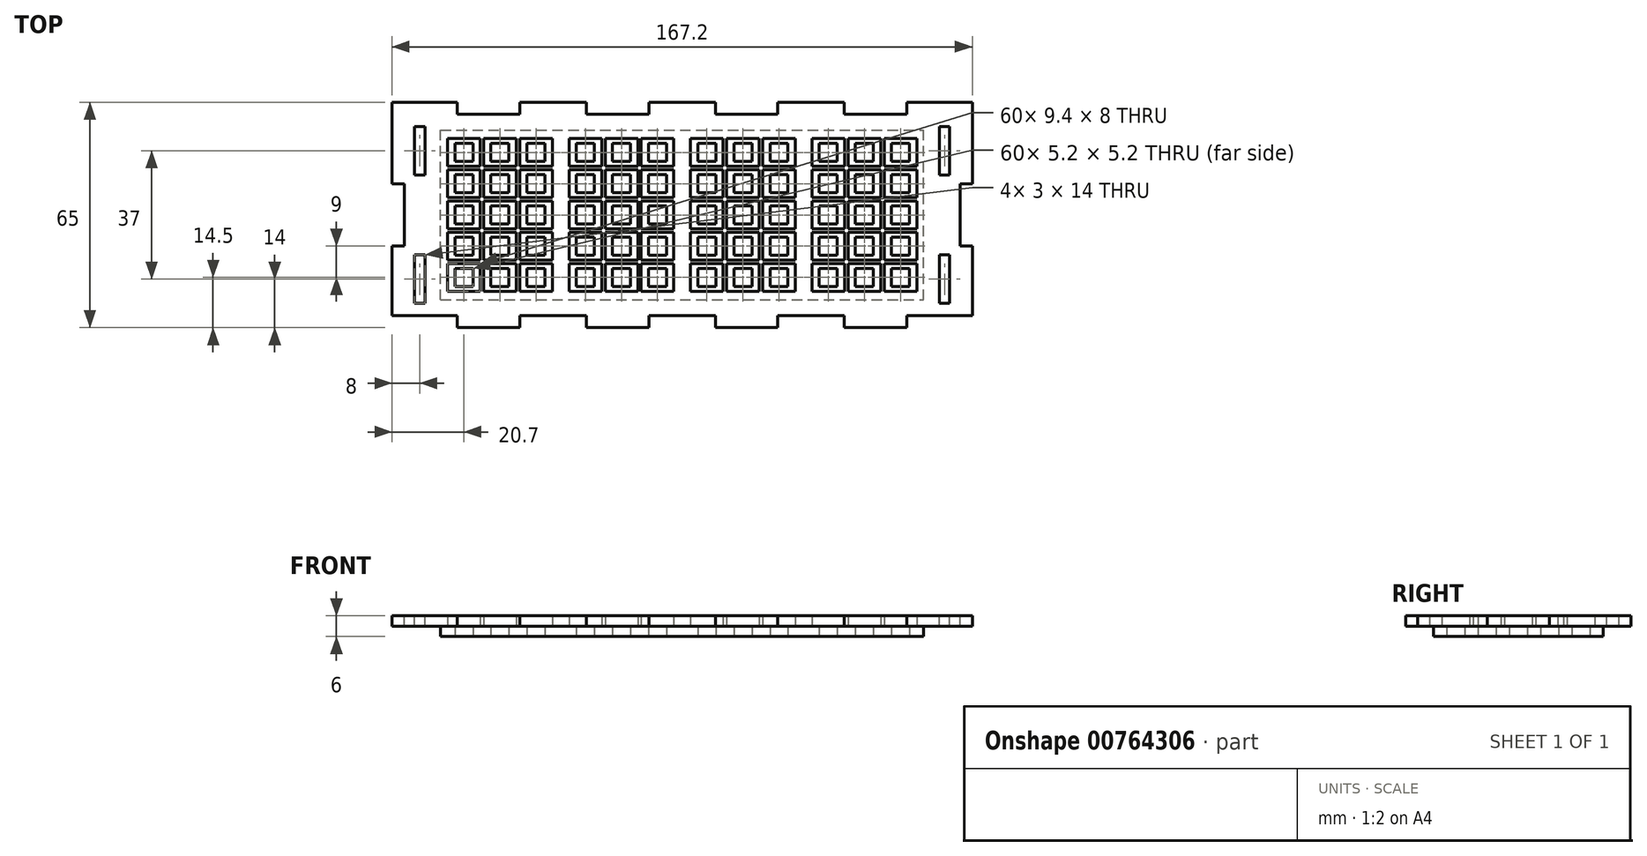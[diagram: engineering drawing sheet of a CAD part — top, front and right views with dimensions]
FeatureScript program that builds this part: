
annotation { "Feature Type Name" : "Feature", "Feature Type Description" : "" }
export const myFeature = defineFeature(function(context is Context, id is Id, definition is map)
    precondition{}
    {
        {
            var Q0;
            Q0=qCreatedBy(makeId("Top.planeOp"),FACE);
            var sketch = newSketch(context, id + "F0", { "sketchPlane" : qUnion([Q0])});
            skLineSegment(sketch, "E0.bottom", {"start": v(0, 0) * mm, "end": v(139.2, 0) * mm});
            skLineSegment(sketch, "E0.left", {"start": v(0, 0) * mm, "end": v(0, 49) * mm});
            skLineSegment(sketch, "E0.right", {"start": v(139.2, 0) * mm, "end": v(139.2, 49) * mm});
            skLineSegment(sketch, "E1.bottom", {"start": v(4.1, 3.9) * mm, "end": v(9.3, 3.9) * mm});
            skLineSegment(sketch, "E1.top", {"start": v(4.1, 9.1) * mm, "end": v(9.3, 9.1) * mm});
            skLineSegment(sketch, "E1.left", {"start": v(4.1, 3.9) * mm, "end": v(4.1, 9.1) * mm});
            skLineSegment(sketch, "E1.right", {"start": v(9.3, 3.9) * mm, "end": v(9.3, 9.1) * mm});
            skLineSegment(sketch, "E2.bottom", {"start": v(39.1, 3.9) * mm, "end": v(44.3, 3.9) * mm});
            skLineSegment(sketch, "E2.top", {"start": v(39.1, 9.1) * mm, "end": v(44.3, 9.1) * mm});
            skLineSegment(sketch, "E2.left", {"start": v(39.1, 3.9) * mm, "end": v(39.1, 9.1) * mm});
            skLineSegment(sketch, "E2.right", {"start": v(44.3, 3.9) * mm, "end": v(44.3, 9.1) * mm});
            skLineSegment(sketch, "E3", {"start": v(0, 49) * mm, "end": v(139.2, 49) * mm});
            skLineSegment(sketch, "E4.bottom", {"start": v(74.1, 3.9) * mm, "end": v(79.3, 3.9) * mm});
            skLineSegment(sketch, "E4.top", {"start": v(74.1, 9.1) * mm, "end": v(79.3, 9.1) * mm});
            skLineSegment(sketch, "E4.left", {"start": v(74.1, 3.9) * mm, "end": v(74.1, 9.1) * mm});
            skLineSegment(sketch, "E4.right", {"start": v(79.3, 3.9) * mm, "end": v(79.3, 9.1) * mm});
            skLineSegment(sketch, "E5.bottom", {"start": v(109.1, 3.9) * mm, "end": v(114.3, 3.9) * mm});
            skLineSegment(sketch, "E5.top", {"start": v(109.1, 9.1) * mm, "end": v(114.3, 9.1) * mm});
            skLineSegment(sketch, "E5.left", {"start": v(109.1, 3.9) * mm, "end": v(109.1, 9.1) * mm});
            skLineSegment(sketch, "E5.right", {"start": v(114.3, 3.9) * mm, "end": v(114.3, 9.1) * mm});
            skLineSegment(sketch, "E6.0.1.0", {"start": v(39.1, 12.9) * mm, "end": v(44.3, 12.9) * mm});
            skLineSegment(sketch, "E6.0.1.1", {"start": v(74.1, 12.9) * mm, "end": v(74.1, 18.1) * mm});
            skLineSegment(sketch, "E6.0.1.2", {"start": v(74.1, 18.1) * mm, "end": v(79.3, 18.1) * mm});
            skLineSegment(sketch, "E6.0.1.3", {"start": v(9.3, 12.9) * mm, "end": v(9.3, 18.1) * mm});
            skLineSegment(sketch, "E6.0.1.4", {"start": v(74.1, 12.9) * mm, "end": v(79.3, 12.9) * mm});
            skLineSegment(sketch, "E6.0.1.5", {"start": v(44.3, 12.9) * mm, "end": v(44.3, 18.1) * mm});
            skLineSegment(sketch, "E6.0.1.6", {"start": v(39.1, 12.9) * mm, "end": v(39.1, 18.1) * mm});
            skLineSegment(sketch, "E6.0.1.7", {"start": v(109.1, 12.9) * mm, "end": v(114.3, 12.9) * mm});
            skLineSegment(sketch, "E6.0.1.8", {"start": v(4.1, 12.9) * mm, "end": v(9.3, 12.9) * mm});
            skLineSegment(sketch, "E6.0.1.9", {"start": v(114.3, 12.9) * mm, "end": v(114.3, 18.1) * mm});
            skLineSegment(sketch, "E6.0.1.10", {"start": v(4.1, 12.9) * mm, "end": v(4.1, 18.1) * mm});
            skLineSegment(sketch, "E6.0.1.11", {"start": v(79.3, 12.9) * mm, "end": v(79.3, 18.1) * mm});
            skLineSegment(sketch, "E6.0.1.12", {"start": v(109.1, 12.9) * mm, "end": v(109.1, 18.1) * mm});
            skLineSegment(sketch, "E6.0.1.13", {"start": v(39.1, 18.1) * mm, "end": v(44.3, 18.1) * mm});
            skLineSegment(sketch, "E6.0.1.14", {"start": v(4.1, 18.1) * mm, "end": v(9.3, 18.1) * mm});
            skLineSegment(sketch, "E6.0.1.15", {"start": v(109.1, 18.1) * mm, "end": v(114.3, 18.1) * mm});
            skLineSegment(sketch, "E6.0.2.0", {"start": v(39.1, 21.9) * mm, "end": v(44.3, 21.9) * mm});
            skLineSegment(sketch, "E6.0.2.1", {"start": v(74.1, 21.9) * mm, "end": v(74.1, 27.1) * mm});
            skLineSegment(sketch, "E6.0.2.2", {"start": v(74.1, 27.1) * mm, "end": v(79.3, 27.1) * mm});
            skLineSegment(sketch, "E6.0.2.3", {"start": v(9.3, 21.9) * mm, "end": v(9.3, 27.1) * mm});
            skLineSegment(sketch, "E6.0.2.4", {"start": v(74.1, 21.9) * mm, "end": v(79.3, 21.9) * mm});
            skLineSegment(sketch, "E6.0.2.5", {"start": v(44.3, 21.9) * mm, "end": v(44.3, 27.1) * mm});
            skLineSegment(sketch, "E6.0.2.6", {"start": v(39.1, 21.9) * mm, "end": v(39.1, 27.1) * mm});
            skLineSegment(sketch, "E6.0.2.7", {"start": v(109.1, 21.9) * mm, "end": v(114.3, 21.9) * mm});
            skLineSegment(sketch, "E6.0.2.8", {"start": v(4.1, 21.9) * mm, "end": v(9.3, 21.9) * mm});
            skLineSegment(sketch, "E6.0.2.9", {"start": v(114.3, 21.9) * mm, "end": v(114.3, 27.1) * mm});
            skLineSegment(sketch, "E6.0.2.10", {"start": v(4.1, 21.9) * mm, "end": v(4.1, 27.1) * mm});
            skLineSegment(sketch, "E6.0.2.11", {"start": v(79.3, 21.9) * mm, "end": v(79.3, 27.1) * mm});
            skLineSegment(sketch, "E6.0.2.12", {"start": v(109.1, 21.9) * mm, "end": v(109.1, 27.1) * mm});
            skLineSegment(sketch, "E6.0.2.13", {"start": v(39.1, 27.1) * mm, "end": v(44.3, 27.1) * mm});
            skLineSegment(sketch, "E6.0.2.14", {"start": v(4.1, 27.1) * mm, "end": v(9.3, 27.1) * mm});
            skLineSegment(sketch, "E6.0.2.15", {"start": v(109.1, 27.1) * mm, "end": v(114.3, 27.1) * mm});
            skLineSegment(sketch, "E6.0.3.0", {"start": v(39.1, 30.9) * mm, "end": v(44.3, 30.9) * mm});
            skLineSegment(sketch, "E6.0.3.1", {"start": v(74.1, 30.9) * mm, "end": v(74.1, 36.1) * mm});
            skLineSegment(sketch, "E6.0.3.2", {"start": v(74.1, 36.1) * mm, "end": v(79.3, 36.1) * mm});
            skLineSegment(sketch, "E6.0.3.3", {"start": v(9.3, 30.9) * mm, "end": v(9.3, 36.1) * mm});
            skLineSegment(sketch, "E6.0.3.4", {"start": v(74.1, 30.9) * mm, "end": v(79.3, 30.9) * mm});
            skLineSegment(sketch, "E6.0.3.5", {"start": v(44.3, 30.9) * mm, "end": v(44.3, 36.1) * mm});
            skLineSegment(sketch, "E6.0.3.6", {"start": v(39.1, 30.9) * mm, "end": v(39.1, 36.1) * mm});
            skLineSegment(sketch, "E6.0.3.7", {"start": v(109.1, 30.9) * mm, "end": v(114.3, 30.9) * mm});
            skLineSegment(sketch, "E6.0.3.8", {"start": v(4.1, 30.9) * mm, "end": v(9.3, 30.9) * mm});
            skLineSegment(sketch, "E6.0.3.9", {"start": v(114.3, 30.9) * mm, "end": v(114.3, 36.1) * mm});
            skLineSegment(sketch, "E6.0.3.10", {"start": v(4.1, 30.9) * mm, "end": v(4.1, 36.1) * mm});
            skLineSegment(sketch, "E6.0.3.11", {"start": v(79.3, 30.9) * mm, "end": v(79.3, 36.1) * mm});
            skLineSegment(sketch, "E6.0.3.12", {"start": v(109.1, 30.9) * mm, "end": v(109.1, 36.1) * mm});
            skLineSegment(sketch, "E6.0.3.13", {"start": v(39.1, 36.1) * mm, "end": v(44.3, 36.1) * mm});
            skLineSegment(sketch, "E6.0.3.14", {"start": v(4.1, 36.1) * mm, "end": v(9.3, 36.1) * mm});
            skLineSegment(sketch, "E6.0.3.15", {"start": v(109.1, 36.1) * mm, "end": v(114.3, 36.1) * mm});
            skLineSegment(sketch, "E6.0.4.0", {"start": v(39.1, 39.9) * mm, "end": v(44.3, 39.9) * mm});
            skLineSegment(sketch, "E6.0.4.1", {"start": v(74.1, 39.9) * mm, "end": v(74.1, 45.1) * mm});
            skLineSegment(sketch, "E6.0.4.2", {"start": v(74.1, 45.1) * mm, "end": v(79.3, 45.1) * mm});
            skLineSegment(sketch, "E6.0.4.3", {"start": v(9.3, 39.9) * mm, "end": v(9.3, 45.1) * mm});
            skLineSegment(sketch, "E6.0.4.4", {"start": v(74.1, 39.9) * mm, "end": v(79.3, 39.9) * mm});
            skLineSegment(sketch, "E6.0.4.5", {"start": v(44.3, 39.9) * mm, "end": v(44.3, 45.1) * mm});
            skLineSegment(sketch, "E6.0.4.6", {"start": v(39.1, 39.9) * mm, "end": v(39.1, 45.1) * mm});
            skLineSegment(sketch, "E6.0.4.7", {"start": v(109.1, 39.9) * mm, "end": v(114.3, 39.9) * mm});
            skLineSegment(sketch, "E6.0.4.8", {"start": v(4.1, 39.9) * mm, "end": v(9.3, 39.9) * mm});
            skLineSegment(sketch, "E6.0.4.9", {"start": v(114.3, 39.9) * mm, "end": v(114.3, 45.1) * mm});
            skLineSegment(sketch, "E6.0.4.10", {"start": v(4.1, 39.9) * mm, "end": v(4.1, 45.1) * mm});
            skLineSegment(sketch, "E6.0.4.11", {"start": v(79.3, 39.9) * mm, "end": v(79.3, 45.1) * mm});
            skLineSegment(sketch, "E6.0.4.12", {"start": v(109.1, 39.9) * mm, "end": v(109.1, 45.1) * mm});
            skLineSegment(sketch, "E6.0.4.13", {"start": v(39.1, 45.1) * mm, "end": v(44.3, 45.1) * mm});
            skLineSegment(sketch, "E6.0.4.14", {"start": v(4.1, 45.1) * mm, "end": v(9.3, 45.1) * mm});
            skLineSegment(sketch, "E6.0.4.15", {"start": v(109.1, 45.1) * mm, "end": v(114.3, 45.1) * mm});
            skLineSegment(sketch, "E6.1.0.0", {"start": v(49.5, 3.9) * mm, "end": v(54.7, 3.9) * mm});
            skLineSegment(sketch, "E6.1.0.1", {"start": v(84.5, 3.9) * mm, "end": v(84.5, 9.1) * mm});
            skLineSegment(sketch, "E6.1.0.2", {"start": v(84.5, 9.1) * mm, "end": v(89.7, 9.1) * mm});
            skLineSegment(sketch, "E6.1.0.3", {"start": v(19.7, 3.9) * mm, "end": v(19.7, 9.1) * mm});
            skLineSegment(sketch, "E6.1.0.4", {"start": v(84.5, 3.9) * mm, "end": v(89.7, 3.9) * mm});
            skLineSegment(sketch, "E6.1.0.5", {"start": v(54.7, 3.9) * mm, "end": v(54.7, 9.1) * mm});
            skLineSegment(sketch, "E6.1.0.6", {"start": v(49.5, 3.9) * mm, "end": v(49.5, 9.1) * mm});
            skLineSegment(sketch, "E6.1.0.7", {"start": v(119.5, 3.9) * mm, "end": v(124.7, 3.9) * mm});
            skLineSegment(sketch, "E6.1.0.8", {"start": v(14.5, 3.9) * mm, "end": v(19.7, 3.9) * mm});
            skLineSegment(sketch, "E6.1.0.9", {"start": v(124.7, 3.9) * mm, "end": v(124.7, 9.1) * mm});
            skLineSegment(sketch, "E6.1.0.10", {"start": v(14.5, 3.9) * mm, "end": v(14.5, 9.1) * mm});
            skLineSegment(sketch, "E6.1.0.11", {"start": v(89.7, 3.9) * mm, "end": v(89.7, 9.1) * mm});
            skLineSegment(sketch, "E6.1.0.12", {"start": v(119.5, 3.9) * mm, "end": v(119.5, 9.1) * mm});
            skLineSegment(sketch, "E6.1.0.13", {"start": v(49.5, 9.1) * mm, "end": v(54.7, 9.1) * mm});
            skLineSegment(sketch, "E6.1.0.14", {"start": v(14.5, 9.1) * mm, "end": v(19.7, 9.1) * mm});
            skLineSegment(sketch, "E6.1.0.15", {"start": v(119.5, 9.1) * mm, "end": v(124.7, 9.1) * mm});
            skLineSegment(sketch, "E6.1.1.0", {"start": v(49.5, 12.9) * mm, "end": v(54.7, 12.9) * mm});
            skLineSegment(sketch, "E6.1.1.1", {"start": v(84.5, 12.9) * mm, "end": v(84.5, 18.1) * mm});
            skLineSegment(sketch, "E6.1.1.2", {"start": v(84.5, 18.1) * mm, "end": v(89.7, 18.1) * mm});
            skLineSegment(sketch, "E6.1.1.3", {"start": v(19.7, 12.9) * mm, "end": v(19.7, 18.1) * mm});
            skLineSegment(sketch, "E6.1.1.4", {"start": v(84.5, 12.9) * mm, "end": v(89.7, 12.9) * mm});
            skLineSegment(sketch, "E6.1.1.5", {"start": v(54.7, 12.9) * mm, "end": v(54.7, 18.1) * mm});
            skLineSegment(sketch, "E6.1.1.6", {"start": v(49.5, 12.9) * mm, "end": v(49.5, 18.1) * mm});
            skLineSegment(sketch, "E6.1.1.7", {"start": v(119.5, 12.9) * mm, "end": v(124.7, 12.9) * mm});
            skLineSegment(sketch, "E6.1.1.8", {"start": v(14.5, 12.9) * mm, "end": v(19.7, 12.9) * mm});
            skLineSegment(sketch, "E6.1.1.9", {"start": v(124.7, 12.9) * mm, "end": v(124.7, 18.1) * mm});
            skLineSegment(sketch, "E6.1.1.10", {"start": v(14.5, 12.9) * mm, "end": v(14.5, 18.1) * mm});
            skLineSegment(sketch, "E6.1.1.11", {"start": v(89.7, 12.9) * mm, "end": v(89.7, 18.1) * mm});
            skLineSegment(sketch, "E6.1.1.12", {"start": v(119.5, 12.9) * mm, "end": v(119.5, 18.1) * mm});
            skLineSegment(sketch, "E6.1.1.13", {"start": v(49.5, 18.1) * mm, "end": v(54.7, 18.1) * mm});
            skLineSegment(sketch, "E6.1.1.14", {"start": v(14.5, 18.1) * mm, "end": v(19.7, 18.1) * mm});
            skLineSegment(sketch, "E6.1.1.15", {"start": v(119.5, 18.1) * mm, "end": v(124.7, 18.1) * mm});
            skLineSegment(sketch, "E6.1.2.0", {"start": v(49.5, 21.9) * mm, "end": v(54.7, 21.9) * mm});
            skLineSegment(sketch, "E6.1.2.1", {"start": v(84.5, 21.9) * mm, "end": v(84.5, 27.1) * mm});
            skLineSegment(sketch, "E6.1.2.2", {"start": v(84.5, 27.1) * mm, "end": v(89.7, 27.1) * mm});
            skLineSegment(sketch, "E6.1.2.3", {"start": v(19.7, 21.9) * mm, "end": v(19.7, 27.1) * mm});
            skLineSegment(sketch, "E6.1.2.4", {"start": v(84.5, 21.9) * mm, "end": v(89.7, 21.9) * mm});
            skLineSegment(sketch, "E6.1.2.5", {"start": v(54.7, 21.9) * mm, "end": v(54.7, 27.1) * mm});
            skLineSegment(sketch, "E6.1.2.6", {"start": v(49.5, 21.9) * mm, "end": v(49.5, 27.1) * mm});
            skLineSegment(sketch, "E6.1.2.7", {"start": v(119.5, 21.9) * mm, "end": v(124.7, 21.9) * mm});
            skLineSegment(sketch, "E6.1.2.8", {"start": v(14.5, 21.9) * mm, "end": v(19.7, 21.9) * mm});
            skLineSegment(sketch, "E6.1.2.9", {"start": v(124.7, 21.9) * mm, "end": v(124.7, 27.1) * mm});
            skLineSegment(sketch, "E6.1.2.10", {"start": v(14.5, 21.9) * mm, "end": v(14.5, 27.1) * mm});
            skLineSegment(sketch, "E6.1.2.11", {"start": v(89.7, 21.9) * mm, "end": v(89.7, 27.1) * mm});
            skLineSegment(sketch, "E6.1.2.12", {"start": v(119.5, 21.9) * mm, "end": v(119.5, 27.1) * mm});
            skLineSegment(sketch, "E6.1.2.13", {"start": v(49.5, 27.1) * mm, "end": v(54.7, 27.1) * mm});
            skLineSegment(sketch, "E6.1.2.14", {"start": v(14.5, 27.1) * mm, "end": v(19.7, 27.1) * mm});
            skLineSegment(sketch, "E6.1.2.15", {"start": v(119.5, 27.1) * mm, "end": v(124.7, 27.1) * mm});
            skLineSegment(sketch, "E6.1.3.0", {"start": v(49.5, 30.9) * mm, "end": v(54.7, 30.9) * mm});
            skLineSegment(sketch, "E6.1.3.1", {"start": v(84.5, 30.9) * mm, "end": v(84.5, 36.1) * mm});
            skLineSegment(sketch, "E6.1.3.2", {"start": v(84.5, 36.1) * mm, "end": v(89.7, 36.1) * mm});
            skLineSegment(sketch, "E6.1.3.3", {"start": v(19.7, 30.9) * mm, "end": v(19.7, 36.1) * mm});
            skLineSegment(sketch, "E6.1.3.4", {"start": v(84.5, 30.9) * mm, "end": v(89.7, 30.9) * mm});
            skLineSegment(sketch, "E6.1.3.5", {"start": v(54.7, 30.9) * mm, "end": v(54.7, 36.1) * mm});
            skLineSegment(sketch, "E6.1.3.6", {"start": v(49.5, 30.9) * mm, "end": v(49.5, 36.1) * mm});
            skLineSegment(sketch, "E6.1.3.7", {"start": v(119.5, 30.9) * mm, "end": v(124.7, 30.9) * mm});
            skLineSegment(sketch, "E6.1.3.8", {"start": v(14.5, 30.9) * mm, "end": v(19.7, 30.9) * mm});
            skLineSegment(sketch, "E6.1.3.9", {"start": v(124.7, 30.9) * mm, "end": v(124.7, 36.1) * mm});
            skLineSegment(sketch, "E6.1.3.10", {"start": v(14.5, 30.9) * mm, "end": v(14.5, 36.1) * mm});
            skLineSegment(sketch, "E6.1.3.11", {"start": v(89.7, 30.9) * mm, "end": v(89.7, 36.1) * mm});
            skLineSegment(sketch, "E6.1.3.12", {"start": v(119.5, 30.9) * mm, "end": v(119.5, 36.1) * mm});
            skLineSegment(sketch, "E6.1.3.13", {"start": v(49.5, 36.1) * mm, "end": v(54.7, 36.1) * mm});
            skLineSegment(sketch, "E6.1.3.14", {"start": v(14.5, 36.1) * mm, "end": v(19.7, 36.1) * mm});
            skLineSegment(sketch, "E6.1.3.15", {"start": v(119.5, 36.1) * mm, "end": v(124.7, 36.1) * mm});
            skLineSegment(sketch, "E6.1.4.0", {"start": v(49.5, 39.9) * mm, "end": v(54.7, 39.9) * mm});
            skLineSegment(sketch, "E6.1.4.1", {"start": v(84.5, 39.9) * mm, "end": v(84.5, 45.1) * mm});
            skLineSegment(sketch, "E6.1.4.2", {"start": v(84.5, 45.1) * mm, "end": v(89.7, 45.1) * mm});
            skLineSegment(sketch, "E6.1.4.3", {"start": v(19.7, 39.9) * mm, "end": v(19.7, 45.1) * mm});
            skLineSegment(sketch, "E6.1.4.4", {"start": v(84.5, 39.9) * mm, "end": v(89.7, 39.9) * mm});
            skLineSegment(sketch, "E6.1.4.5", {"start": v(54.7, 39.9) * mm, "end": v(54.7, 45.1) * mm});
            skLineSegment(sketch, "E6.1.4.6", {"start": v(49.5, 39.9) * mm, "end": v(49.5, 45.1) * mm});
            skLineSegment(sketch, "E6.1.4.7", {"start": v(119.5, 39.9) * mm, "end": v(124.7, 39.9) * mm});
            skLineSegment(sketch, "E6.1.4.8", {"start": v(14.5, 39.9) * mm, "end": v(19.7, 39.9) * mm});
            skLineSegment(sketch, "E6.1.4.9", {"start": v(124.7, 39.9) * mm, "end": v(124.7, 45.1) * mm});
            skLineSegment(sketch, "E6.1.4.10", {"start": v(14.5, 39.9) * mm, "end": v(14.5, 45.1) * mm});
            skLineSegment(sketch, "E6.1.4.11", {"start": v(89.7, 39.9) * mm, "end": v(89.7, 45.1) * mm});
            skLineSegment(sketch, "E6.1.4.12", {"start": v(119.5, 39.9) * mm, "end": v(119.5, 45.1) * mm});
            skLineSegment(sketch, "E6.1.4.13", {"start": v(49.5, 45.1) * mm, "end": v(54.7, 45.1) * mm});
            skLineSegment(sketch, "E6.1.4.14", {"start": v(14.5, 45.1) * mm, "end": v(19.7, 45.1) * mm});
            skLineSegment(sketch, "E6.1.4.15", {"start": v(119.5, 45.1) * mm, "end": v(124.7, 45.1) * mm});
            skLineSegment(sketch, "E6.2.0.0", {"start": v(59.9, 3.9) * mm, "end": v(65.1, 3.9) * mm});
            skLineSegment(sketch, "E6.2.0.1", {"start": v(94.9, 3.9) * mm, "end": v(94.9, 9.1) * mm});
            skLineSegment(sketch, "E6.2.0.2", {"start": v(94.9, 9.1) * mm, "end": v(100.1, 9.1) * mm});
            skLineSegment(sketch, "E6.2.0.3", {"start": v(30.1, 3.9) * mm, "end": v(30.1, 9.1) * mm});
            skLineSegment(sketch, "E6.2.0.4", {"start": v(94.9, 3.9) * mm, "end": v(100.1, 3.9) * mm});
            skLineSegment(sketch, "E6.2.0.5", {"start": v(65.1, 3.9) * mm, "end": v(65.1, 9.1) * mm});
            skLineSegment(sketch, "E6.2.0.6", {"start": v(59.9, 3.9) * mm, "end": v(59.9, 9.1) * mm});
            skLineSegment(sketch, "E6.2.0.7", {"start": v(129.9, 3.9) * mm, "end": v(135.1, 3.9) * mm});
            skLineSegment(sketch, "E6.2.0.8", {"start": v(24.9, 3.9) * mm, "end": v(30.1, 3.9) * mm});
            skLineSegment(sketch, "E6.2.0.9", {"start": v(135.1, 3.9) * mm, "end": v(135.1, 9.1) * mm});
            skLineSegment(sketch, "E6.2.0.10", {"start": v(24.9, 3.9) * mm, "end": v(24.9, 9.1) * mm});
            skLineSegment(sketch, "E6.2.0.11", {"start": v(100.1, 3.9) * mm, "end": v(100.1, 9.1) * mm});
            skLineSegment(sketch, "E6.2.0.12", {"start": v(129.9, 3.9) * mm, "end": v(129.9, 9.1) * mm});
            skLineSegment(sketch, "E6.2.0.13", {"start": v(59.9, 9.1) * mm, "end": v(65.1, 9.1) * mm});
            skLineSegment(sketch, "E6.2.0.14", {"start": v(24.9, 9.1) * mm, "end": v(30.1, 9.1) * mm});
            skLineSegment(sketch, "E6.2.0.15", {"start": v(129.9, 9.1) * mm, "end": v(135.1, 9.1) * mm});
            skLineSegment(sketch, "E6.2.1.0", {"start": v(59.9, 12.9) * mm, "end": v(65.1, 12.9) * mm});
            skLineSegment(sketch, "E6.2.1.1", {"start": v(94.9, 12.9) * mm, "end": v(94.9, 18.1) * mm});
            skLineSegment(sketch, "E6.2.1.2", {"start": v(94.9, 18.1) * mm, "end": v(100.1, 18.1) * mm});
            skLineSegment(sketch, "E6.2.1.3", {"start": v(30.1, 12.9) * mm, "end": v(30.1, 18.1) * mm});
            skLineSegment(sketch, "E6.2.1.4", {"start": v(94.9, 12.9) * mm, "end": v(100.1, 12.9) * mm});
            skLineSegment(sketch, "E6.2.1.5", {"start": v(65.1, 12.9) * mm, "end": v(65.1, 18.1) * mm});
            skLineSegment(sketch, "E6.2.1.6", {"start": v(59.9, 12.9) * mm, "end": v(59.9, 18.1) * mm});
            skLineSegment(sketch, "E6.2.1.7", {"start": v(129.9, 12.9) * mm, "end": v(135.1, 12.9) * mm});
            skLineSegment(sketch, "E6.2.1.8", {"start": v(24.9, 12.9) * mm, "end": v(30.1, 12.9) * mm});
            skLineSegment(sketch, "E6.2.1.9", {"start": v(135.1, 12.9) * mm, "end": v(135.1, 18.1) * mm});
            skLineSegment(sketch, "E6.2.1.10", {"start": v(24.9, 12.9) * mm, "end": v(24.9, 18.1) * mm});
            skLineSegment(sketch, "E6.2.1.11", {"start": v(100.1, 12.9) * mm, "end": v(100.1, 18.1) * mm});
            skLineSegment(sketch, "E6.2.1.12", {"start": v(129.9, 12.9) * mm, "end": v(129.9, 18.1) * mm});
            skLineSegment(sketch, "E6.2.1.13", {"start": v(59.9, 18.1) * mm, "end": v(65.1, 18.1) * mm});
            skLineSegment(sketch, "E6.2.1.14", {"start": v(24.9, 18.1) * mm, "end": v(30.1, 18.1) * mm});
            skLineSegment(sketch, "E6.2.1.15", {"start": v(129.9, 18.1) * mm, "end": v(135.1, 18.1) * mm});
            skLineSegment(sketch, "E6.2.2.0", {"start": v(59.9, 21.9) * mm, "end": v(65.1, 21.9) * mm});
            skLineSegment(sketch, "E6.2.2.1", {"start": v(94.9, 21.9) * mm, "end": v(94.9, 27.1) * mm});
            skLineSegment(sketch, "E6.2.2.2", {"start": v(94.9, 27.1) * mm, "end": v(100.1, 27.1) * mm});
            skLineSegment(sketch, "E6.2.2.3", {"start": v(30.1, 21.9) * mm, "end": v(30.1, 27.1) * mm});
            skLineSegment(sketch, "E6.2.2.4", {"start": v(94.9, 21.9) * mm, "end": v(100.1, 21.9) * mm});
            skLineSegment(sketch, "E6.2.2.5", {"start": v(65.1, 21.9) * mm, "end": v(65.1, 27.1) * mm});
            skLineSegment(sketch, "E6.2.2.6", {"start": v(59.9, 21.9) * mm, "end": v(59.9, 27.1) * mm});
            skLineSegment(sketch, "E6.2.2.7", {"start": v(129.9, 21.9) * mm, "end": v(135.1, 21.9) * mm});
            skLineSegment(sketch, "E6.2.2.8", {"start": v(24.9, 21.9) * mm, "end": v(30.1, 21.9) * mm});
            skLineSegment(sketch, "E6.2.2.9", {"start": v(135.1, 21.9) * mm, "end": v(135.1, 27.1) * mm});
            skLineSegment(sketch, "E6.2.2.10", {"start": v(24.9, 21.9) * mm, "end": v(24.9, 27.1) * mm});
            skLineSegment(sketch, "E6.2.2.11", {"start": v(100.1, 21.9) * mm, "end": v(100.1, 27.1) * mm});
            skLineSegment(sketch, "E6.2.2.12", {"start": v(129.9, 21.9) * mm, "end": v(129.9, 27.1) * mm});
            skLineSegment(sketch, "E6.2.2.13", {"start": v(59.9, 27.1) * mm, "end": v(65.1, 27.1) * mm});
            skLineSegment(sketch, "E6.2.2.14", {"start": v(24.9, 27.1) * mm, "end": v(30.1, 27.1) * mm});
            skLineSegment(sketch, "E6.2.2.15", {"start": v(129.9, 27.1) * mm, "end": v(135.1, 27.1) * mm});
            skLineSegment(sketch, "E6.2.3.0", {"start": v(59.9, 30.9) * mm, "end": v(65.1, 30.9) * mm});
            skLineSegment(sketch, "E6.2.3.1", {"start": v(94.9, 30.9) * mm, "end": v(94.9, 36.1) * mm});
            skLineSegment(sketch, "E6.2.3.2", {"start": v(94.9, 36.1) * mm, "end": v(100.1, 36.1) * mm});
            skLineSegment(sketch, "E6.2.3.3", {"start": v(30.1, 30.9) * mm, "end": v(30.1, 36.1) * mm});
            skLineSegment(sketch, "E6.2.3.4", {"start": v(94.9, 30.9) * mm, "end": v(100.1, 30.9) * mm});
            skLineSegment(sketch, "E6.2.3.5", {"start": v(65.1, 30.9) * mm, "end": v(65.1, 36.1) * mm});
            skLineSegment(sketch, "E6.2.3.6", {"start": v(59.9, 30.9) * mm, "end": v(59.9, 36.1) * mm});
            skLineSegment(sketch, "E6.2.3.7", {"start": v(129.9, 30.9) * mm, "end": v(135.1, 30.9) * mm});
            skLineSegment(sketch, "E6.2.3.8", {"start": v(24.9, 30.9) * mm, "end": v(30.1, 30.9) * mm});
            skLineSegment(sketch, "E6.2.3.9", {"start": v(135.1, 30.9) * mm, "end": v(135.1, 36.1) * mm});
            skLineSegment(sketch, "E6.2.3.10", {"start": v(24.9, 30.9) * mm, "end": v(24.9, 36.1) * mm});
            skLineSegment(sketch, "E6.2.3.11", {"start": v(100.1, 30.9) * mm, "end": v(100.1, 36.1) * mm});
            skLineSegment(sketch, "E6.2.3.12", {"start": v(129.9, 30.9) * mm, "end": v(129.9, 36.1) * mm});
            skLineSegment(sketch, "E6.2.3.13", {"start": v(59.9, 36.1) * mm, "end": v(65.1, 36.1) * mm});
            skLineSegment(sketch, "E6.2.3.14", {"start": v(24.9, 36.1) * mm, "end": v(30.1, 36.1) * mm});
            skLineSegment(sketch, "E6.2.3.15", {"start": v(129.9, 36.1) * mm, "end": v(135.1, 36.1) * mm});
            skLineSegment(sketch, "E6.2.4.0", {"start": v(59.9, 39.9) * mm, "end": v(65.1, 39.9) * mm});
            skLineSegment(sketch, "E6.2.4.1", {"start": v(94.9, 39.9) * mm, "end": v(94.9, 45.1) * mm});
            skLineSegment(sketch, "E6.2.4.2", {"start": v(94.9, 45.1) * mm, "end": v(100.1, 45.1) * mm});
            skLineSegment(sketch, "E6.2.4.3", {"start": v(30.1, 39.9) * mm, "end": v(30.1, 45.1) * mm});
            skLineSegment(sketch, "E6.2.4.4", {"start": v(94.9, 39.9) * mm, "end": v(100.1, 39.9) * mm});
            skLineSegment(sketch, "E6.2.4.5", {"start": v(65.1, 39.9) * mm, "end": v(65.1, 45.1) * mm});
            skLineSegment(sketch, "E6.2.4.6", {"start": v(59.9, 39.9) * mm, "end": v(59.9, 45.1) * mm});
            skLineSegment(sketch, "E6.2.4.7", {"start": v(129.9, 39.9) * mm, "end": v(135.1, 39.9) * mm});
            skLineSegment(sketch, "E6.2.4.8", {"start": v(24.9, 39.9) * mm, "end": v(30.1, 39.9) * mm});
            skLineSegment(sketch, "E6.2.4.9", {"start": v(135.1, 39.9) * mm, "end": v(135.1, 45.1) * mm});
            skLineSegment(sketch, "E6.2.4.10", {"start": v(24.9, 39.9) * mm, "end": v(24.9, 45.1) * mm});
            skLineSegment(sketch, "E6.2.4.11", {"start": v(100.1, 39.9) * mm, "end": v(100.1, 45.1) * mm});
            skLineSegment(sketch, "E6.2.4.12", {"start": v(129.9, 39.9) * mm, "end": v(129.9, 45.1) * mm});
            skLineSegment(sketch, "E6.2.4.13", {"start": v(59.9, 45.1) * mm, "end": v(65.1, 45.1) * mm});
            skLineSegment(sketch, "E6.2.4.14", {"start": v(24.9, 45.1) * mm, "end": v(30.1, 45.1) * mm});
            skLineSegment(sketch, "E6.2.4.15", {"start": v(129.9, 45.1) * mm, "end": v(135.1, 45.1) * mm});
            skLineSegment(sketch, "E6.direction1", {"start": v(4.1, 3.9) * mm, "end": v(14.5, 3.9) * mm, "construction": true});
            skLineSegment(sketch, "E6.direction2", {"start": v(4.1, 3.9) * mm, "end": v(4.1, 12.9) * mm, "construction": true});
            skSolve(sketch);
        }
        {
            var Q0;
            Q0=makeQuery(id+"F0.imprint","IMPRINT",FACE,{"disambiguationData":[TD([[makeQuery(id+"F0.imprint","IMPRINT",EDGE,{"derivedFrom":sQuery(id+"F0.wireOp",EDGE,"E0.bottom")}),1.0]])]});
            extrude(context, id + "F1", {"entities" : qUnion([Q0]), "depth" : 3 * mm, "offsetDistance" : 25 * mm});
        }
        {
            var Q0;
            Q0=makeQuery(id+"F1.opExtrude","CAP_FACE",FACE,{"disambiguationData":[OSD([sQuery(id+"F0.wireOp",EDGE,"E0.bottom"),sQuery(id+"F0.wireOp",EDGE,"E0.top"),sQuery(id+"F0.wireOp",EDGE,"E0.left"),sQuery(id+"F0.wireOp",EDGE,"E0.right"),sQuery(id+"F0.wireOp",EDGE,"E1.bottom"),sQuery(id+"F0.wireOp",EDGE,"E1.top"),sQuery(id+"F0.wireOp",EDGE,"E1.left"),sQuery(id+"F0.wireOp",EDGE,"E1.right"),sQuery(id+"F0.wireOp",EDGE,"95869116-3487-4177-9028-07c310471c4a.0.1.0"),sQuery(id+"F0.wireOp",EDGE,"95869116-3487-4177-9028-07c310471c4a.0.1.1"),sQuery(id+"F0.wireOp",EDGE,"95869116-3487-4177-9028-07c310471c4a.0.1.2"),sQuery(id+"F0.wireOp",EDGE,"95869116-3487-4177-9028-07c310471c4a.0.1.3"),sQuery(id+"F0.wireOp",EDGE,"95869116-3487-4177-9028-07c310471c4a.0.2.0"),sQuery(id+"F0.wireOp",EDGE,"95869116-3487-4177-9028-07c310471c4a.0.2.1"),sQuery(id+"F0.wireOp",EDGE,"95869116-3487-4177-9028-07c310471c4a.0.2.2"),sQuery(id+"F0.wireOp",EDGE,"95869116-3487-4177-9028-07c310471c4a.0.2.3"),sQuery(id+"F0.wireOp",EDGE,"95869116-3487-4177-9028-07c310471c4a.0.3.0"),sQuery(id+"F0.wireOp",EDGE,"95869116-3487-4177-9028-07c310471c4a.0.3.1"),sQuery(id+"F0.wireOp",EDGE,"95869116-3487-4177-9028-07c310471c4a.0.3.2"),sQuery(id+"F0.wireOp",EDGE,"95869116-3487-4177-9028-07c310471c4a.0.3.3"),sQuery(id+"F0.wireOp",EDGE,"95869116-3487-4177-9028-07c310471c4a.0.4.0"),sQuery(id+"F0.wireOp",EDGE,"95869116-3487-4177-9028-07c310471c4a.0.4.1"),sQuery(id+"F0.wireOp",EDGE,"95869116-3487-4177-9028-07c310471c4a.0.4.2"),sQuery(id+"F0.wireOp",EDGE,"95869116-3487-4177-9028-07c310471c4a.0.4.3"),sQuery(id+"F0.wireOp",EDGE,"95869116-3487-4177-9028-07c310471c4a.1.0.0"),sQuery(id+"F0.wireOp",EDGE,"95869116-3487-4177-9028-07c310471c4a.1.0.1"),sQuery(id+"F0.wireOp",EDGE,"95869116-3487-4177-9028-07c310471c4a.1.0.2"),sQuery(id+"F0.wireOp",EDGE,"95869116-3487-4177-9028-07c310471c4a.1.0.3"),sQuery(id+"F0.wireOp",EDGE,"95869116-3487-4177-9028-07c310471c4a.1.1.0"),sQuery(id+"F0.wireOp",EDGE,"95869116-3487-4177-9028-07c310471c4a.1.1.1"),sQuery(id+"F0.wireOp",EDGE,"95869116-3487-4177-9028-07c310471c4a.1.1.2"),sQuery(id+"F0.wireOp",EDGE,"95869116-3487-4177-9028-07c310471c4a.1.1.3"),sQuery(id+"F0.wireOp",EDGE,"95869116-3487-4177-9028-07c310471c4a.1.2.0"),sQuery(id+"F0.wireOp",EDGE,"95869116-3487-4177-9028-07c310471c4a.1.2.1"),sQuery(id+"F0.wireOp",EDGE,"95869116-3487-4177-9028-07c310471c4a.1.2.2"),sQuery(id+"F0.wireOp",EDGE,"95869116-3487-4177-9028-07c310471c4a.1.2.3"),sQuery(id+"F0.wireOp",EDGE,"95869116-3487-4177-9028-07c310471c4a.1.3.0"),sQuery(id+"F0.wireOp",EDGE,"95869116-3487-4177-9028-07c310471c4a.1.3.1"),sQuery(id+"F0.wireOp",EDGE,"95869116-3487-4177-9028-07c310471c4a.1.3.2"),sQuery(id+"F0.wireOp",EDGE,"95869116-3487-4177-9028-07c310471c4a.1.3.3"),sQuery(id+"F0.wireOp",EDGE,"95869116-3487-4177-9028-07c310471c4a.1.4.0"),sQuery(id+"F0.wireOp",EDGE,"95869116-3487-4177-9028-07c310471c4a.1.4.1"),sQuery(id+"F0.wireOp",EDGE,"95869116-3487-4177-9028-07c310471c4a.1.4.2"),sQuery(id+"F0.wireOp",EDGE,"95869116-3487-4177-9028-07c310471c4a.1.4.3"),sQuery(id+"F0.wireOp",EDGE,"95869116-3487-4177-9028-07c310471c4a.2.0.0"),sQuery(id+"F0.wireOp",EDGE,"95869116-3487-4177-9028-07c310471c4a.2.0.1"),sQuery(id+"F0.wireOp",EDGE,"95869116-3487-4177-9028-07c310471c4a.2.0.2"),sQuery(id+"F0.wireOp",EDGE,"95869116-3487-4177-9028-07c310471c4a.2.0.3"),sQuery(id+"F0.wireOp",EDGE,"95869116-3487-4177-9028-07c310471c4a.2.1.0"),sQuery(id+"F0.wireOp",EDGE,"95869116-3487-4177-9028-07c310471c4a.2.1.1"),sQuery(id+"F0.wireOp",EDGE,"95869116-3487-4177-9028-07c310471c4a.2.1.2"),sQuery(id+"F0.wireOp",EDGE,"95869116-3487-4177-9028-07c310471c4a.2.1.3"),sQuery(id+"F0.wireOp",EDGE,"95869116-3487-4177-9028-07c310471c4a.2.2.0"),sQuery(id+"F0.wireOp",EDGE,"95869116-3487-4177-9028-07c310471c4a.2.2.1"),sQuery(id+"F0.wireOp",EDGE,"95869116-3487-4177-9028-07c310471c4a.2.2.2"),sQuery(id+"F0.wireOp",EDGE,"95869116-3487-4177-9028-07c310471c4a.2.2.3"),sQuery(id+"F0.wireOp",EDGE,"95869116-3487-4177-9028-07c310471c4a.2.3.0"),sQuery(id+"F0.wireOp",EDGE,"95869116-3487-4177-9028-07c310471c4a.2.3.1"),sQuery(id+"F0.wireOp",EDGE,"95869116-3487-4177-9028-07c310471c4a.2.3.2"),sQuery(id+"F0.wireOp",EDGE,"95869116-3487-4177-9028-07c310471c4a.2.3.3"),sQuery(id+"F0.wireOp",EDGE,"95869116-3487-4177-9028-07c310471c4a.2.4.0"),sQuery(id+"F0.wireOp",EDGE,"95869116-3487-4177-9028-07c310471c4a.2.4.1"),sQuery(id+"F0.wireOp",EDGE,"95869116-3487-4177-9028-07c310471c4a.2.4.2"),sQuery(id+"F0.wireOp",EDGE,"95869116-3487-4177-9028-07c310471c4a.2.4.3"),sQuery(id+"F0.wireOp",EDGE,"49dafa04-c45d-4b5c-802c-71c5818911b00.MirrorCS"),sQuery(id+"F0.wireOp",EDGE,"49dafa04-c45d-4b5c-802c-71c5818911b01.MirrorCS"),sQuery(id+"F0.wireOp",EDGE,"49dafa04-c45d-4b5c-802c-71c5818911b02.MirrorCS"),sQuery(id+"F0.wireOp",EDGE,"49dafa04-c45d-4b5c-802c-71c5818911b03.MirrorCS"),sQuery(id+"F0.wireOp",EDGE,"49dafa04-c45d-4b5c-802c-71c5818911b04.MirrorCS"),sQuery(id+"F0.wireOp",EDGE,"49dafa04-c45d-4b5c-802c-71c5818911b05.MirrorCS"),sQuery(id+"F0.wireOp",EDGE,"49dafa04-c45d-4b5c-802c-71c5818911b07.MirrorCS"),sQuery(id+"F0.wireOp",EDGE,"49dafa04-c45d-4b5c-802c-71c5818911b08.MirrorCS"),sQuery(id+"F0.wireOp",EDGE,"49dafa04-c45d-4b5c-802c-71c5818911b09.MirrorCS"),sQuery(id+"F0.wireOp",EDGE,"49dafa04-c45d-4b5c-802c-71c5818911b010.MirrorCS"),sQuery(id+"F0.wireOp",EDGE,"49dafa04-c45d-4b5c-802c-71c5818911b011.MirrorCS"),sQuery(id+"F0.wireOp",EDGE,"49dafa04-c45d-4b5c-802c-71c5818911b012.MirrorCS"),sQuery(id+"F0.wireOp",EDGE,"49dafa04-c45d-4b5c-802c-71c5818911b013.MirrorCS"),sQuery(id+"F0.wireOp",EDGE,"49dafa04-c45d-4b5c-802c-71c5818911b014.MirrorCS"),sQuery(id+"F0.wireOp",EDGE,"49dafa04-c45d-4b5c-802c-71c5818911b015.MirrorCS"),sQuery(id+"F0.wireOp",EDGE,"49dafa04-c45d-4b5c-802c-71c5818911b016.MirrorCS"),sQuery(id+"F0.wireOp",EDGE,"49dafa04-c45d-4b5c-802c-71c5818911b017.MirrorCS"),sQuery(id+"F0.wireOp",EDGE,"49dafa04-c45d-4b5c-802c-71c5818911b018.MirrorCS"),sQuery(id+"F0.wireOp",EDGE,"49dafa04-c45d-4b5c-802c-71c5818911b019.MirrorCS"),sQuery(id+"F0.wireOp",EDGE,"49dafa04-c45d-4b5c-802c-71c5818911b020.MirrorCS"),sQuery(id+"F0.wireOp",EDGE,"49dafa04-c45d-4b5c-802c-71c5818911b021.MirrorCS"),sQuery(id+"F0.wireOp",EDGE,"49dafa04-c45d-4b5c-802c-71c5818911b024.MirrorCS"),sQuery(id+"F0.wireOp",EDGE,"49dafa04-c45d-4b5c-802c-71c5818911b025.MirrorCS"),sQuery(id+"F0.wireOp",EDGE,"49dafa04-c45d-4b5c-802c-71c5818911b026.MirrorCS"),sQuery(id+"F0.wireOp",EDGE,"49dafa04-c45d-4b5c-802c-71c5818911b027.MirrorCS"),sQuery(id+"F0.wireOp",EDGE,"49dafa04-c45d-4b5c-802c-71c5818911b028.MirrorCS"),sQuery(id+"F0.wireOp",EDGE,"49dafa04-c45d-4b5c-802c-71c5818911b029.MirrorCS"),sQuery(id+"F0.wireOp",EDGE,"49dafa04-c45d-4b5c-802c-71c5818911b030.MirrorCS"),sQuery(id+"F0.wireOp",EDGE,"49dafa04-c45d-4b5c-802c-71c5818911b031.MirrorCS"),sQuery(id+"F0.wireOp",EDGE,"49dafa04-c45d-4b5c-802c-71c5818911b032.MirrorCS"),sQuery(id+"F0.wireOp",EDGE,"49dafa04-c45d-4b5c-802c-71c5818911b033.MirrorCS"),sQuery(id+"F0.wireOp",EDGE,"49dafa04-c45d-4b5c-802c-71c5818911b034.MirrorCS"),sQuery(id+"F0.wireOp",EDGE,"49dafa04-c45d-4b5c-802c-71c5818911b035.MirrorCS"),sQuery(id+"F0.wireOp",EDGE,"49dafa04-c45d-4b5c-802c-71c5818911b036.MirrorCS"),sQuery(id+"F0.wireOp",EDGE,"49dafa04-c45d-4b5c-802c-71c5818911b037.MirrorCS"),sQuery(id+"F0.wireOp",EDGE,"49dafa04-c45d-4b5c-802c-71c5818911b038.MirrorCS"),sQuery(id+"F0.wireOp",EDGE,"49dafa04-c45d-4b5c-802c-71c5818911b039.MirrorCS"),sQuery(id+"F0.wireOp",EDGE,"49dafa04-c45d-4b5c-802c-71c5818911b040.MirrorCS"),sQuery(id+"F0.wireOp",EDGE,"49dafa04-c45d-4b5c-802c-71c5818911b041.MirrorCS"),sQuery(id+"F0.wireOp",EDGE,"49dafa04-c45d-4b5c-802c-71c5818911b042.MirrorCS"),sQuery(id+"F0.wireOp",EDGE,"49dafa04-c45d-4b5c-802c-71c5818911b043.MirrorCS"),sQuery(id+"F0.wireOp",EDGE,"49dafa04-c45d-4b5c-802c-71c5818911b044.MirrorCS"),sQuery(id+"F0.wireOp",EDGE,"49dafa04-c45d-4b5c-802c-71c5818911b045.MirrorCS"),sQuery(id+"F0.wireOp",EDGE,"49dafa04-c45d-4b5c-802c-71c5818911b046.MirrorCS"),sQuery(id+"F0.wireOp",EDGE,"49dafa04-c45d-4b5c-802c-71c5818911b047.MirrorCS"),sQuery(id+"F0.wireOp",EDGE,"49dafa04-c45d-4b5c-802c-71c5818911b048.MirrorCS"),sQuery(id+"F0.wireOp",EDGE,"49dafa04-c45d-4b5c-802c-71c5818911b049.MirrorCS"),sQuery(id+"F0.wireOp",EDGE,"49dafa04-c45d-4b5c-802c-71c5818911b050.MirrorCS"),sQuery(id+"F0.wireOp",EDGE,"49dafa04-c45d-4b5c-802c-71c5818911b051.MirrorCS"),sQuery(id+"F0.wireOp",EDGE,"49dafa04-c45d-4b5c-802c-71c5818911b052.MirrorCS"),sQuery(id+"F0.wireOp",EDGE,"49dafa04-c45d-4b5c-802c-71c5818911b053.MirrorCS"),sQuery(id+"F0.wireOp",EDGE,"49dafa04-c45d-4b5c-802c-71c5818911b054.MirrorCS"),sQuery(id+"F0.wireOp",EDGE,"49dafa04-c45d-4b5c-802c-71c5818911b055.MirrorCS"),sQuery(id+"F0.wireOp",EDGE,"49dafa04-c45d-4b5c-802c-71c5818911b056.MirrorCS"),sQuery(id+"F0.wireOp",EDGE,"49dafa04-c45d-4b5c-802c-71c5818911b057.MirrorCS"),sQuery(id+"F0.wireOp",EDGE,"49dafa04-c45d-4b5c-802c-71c5818911b058.MirrorCS"),sQuery(id+"F0.wireOp",EDGE,"49dafa04-c45d-4b5c-802c-71c5818911b059.MirrorCS"),sQuery(id+"F0.wireOp",EDGE,"49dafa04-c45d-4b5c-802c-71c5818911b060.MirrorCS"),sQuery(id+"F0.wireOp",EDGE,"49dafa04-c45d-4b5c-802c-71c5818911b061.MirrorCS"),sQuery(id+"F0.wireOp",EDGE,"49dafa04-c45d-4b5c-802c-71c5818911b062.MirrorCS")])],"isStart":false});
            var sketch = newSketch(context, id + "F2", { "sketchPlane" : qUnion([Q0])});
            skLineSegment(sketch, "E7.bottom", {"start": v(-14, -8) * mm, "end": v(153.2, -8) * mm});
            skLineSegment(sketch, "E7.top", {"start": v(-14, 57) * mm, "end": v(153.2, 57) * mm});
            skLineSegment(sketch, "E7.left", {"start": v(-14, -8) * mm, "end": v(-14, 57) * mm});
            skLineSegment(sketch, "E7.right", {"start": v(153.2, -8) * mm, "end": v(153.2, 57) * mm});
            skLineSegment(sketch, "E8", {"start": v(69.6, -8) * mm, "end": v(69.6, 0) * mm, "construction": true});
            skLineSegment(sketch, "E9.bottom", {"start": v(2, 2.5) * mm, "end": v(11.4, 2.5) * mm});
            skLineSegment(sketch, "E9.top", {"start": v(2, 10.5) * mm, "end": v(11.4, 10.5) * mm});
            skLineSegment(sketch, "E9.left", {"start": v(2, 2.5) * mm, "end": v(2, 10.5) * mm});
            skLineSegment(sketch, "E9.right", {"start": v(11.4, 2.5) * mm, "end": v(11.4, 10.5) * mm});
            skLineSegment(sketch, "E10.bottom", {"start": v(37, 2.5) * mm, "end": v(46.4, 2.5) * mm});
            skLineSegment(sketch, "E10.top", {"start": v(37, 10.5) * mm, "end": v(46.4, 10.5) * mm});
            skLineSegment(sketch, "E10.left", {"start": v(37, 2.5) * mm, "end": v(37, 10.5) * mm});
            skLineSegment(sketch, "E10.right", {"start": v(46.4, 2.5) * mm, "end": v(46.4, 10.5) * mm});
            skLineSegment(sketch, "E11", {"start": v(6.7, 2.5) * mm, "end": v(6.7, 3.9) * mm, "construction": true});
            skLineSegment(sketch, "E12", {"start": v(2, 6.5) * mm, "end": v(4.1, 6.5) * mm, "construction": true});
            skLineSegment(sketch, "E13", {"start": v(41.7, 2.5) * mm, "end": v(41.7, 3.9) * mm, "construction": true});
            skPoint(sketch, "E13.startSnap0", {"position": v(41.7, 3.9) * mm});
            skPoint(sketch, "E13.startSnap1", {"position": v(41.7, 2.5) * mm});
            skLineSegment(sketch, "E14", {"start": v(37, 6.5) * mm, "end": v(39.1, 6.5) * mm, "construction": true});
            skLineSegment(sketch, "E15.bottom", {"start": v(72, 2.5) * mm, "end": v(81.4, 2.5) * mm});
            skLineSegment(sketch, "E15.top", {"start": v(72, 10.5) * mm, "end": v(81.4, 10.5) * mm});
            skLineSegment(sketch, "E15.left", {"start": v(72, 2.5) * mm, "end": v(72, 10.5) * mm});
            skLineSegment(sketch, "E15.right", {"start": v(81.4, 2.5) * mm, "end": v(81.4, 10.5) * mm});
            skLineSegment(sketch, "E16.bottom", {"start": v(107, 2.5) * mm, "end": v(116.4, 2.5) * mm});
            skLineSegment(sketch, "E16.top", {"start": v(107, 10.5) * mm, "end": v(116.4, 10.5) * mm});
            skLineSegment(sketch, "E16.left", {"start": v(107, 2.5) * mm, "end": v(107, 10.5) * mm});
            skLineSegment(sketch, "E16.right", {"start": v(116.4, 2.5) * mm, "end": v(116.4, 10.5) * mm});
            skLineSegment(sketch, "E17", {"start": v(76.7, 3.9) * mm, "end": v(76.7, 2.5) * mm, "construction": true});
            skLineSegment(sketch, "E18", {"start": v(74.1, 6.5) * mm, "end": v(72, 6.5) * mm, "construction": true});
            skLineSegment(sketch, "E19", {"start": v(111.7, 3.9) * mm, "end": v(111.7, 2.5) * mm, "construction": true});
            skLineSegment(sketch, "E20", {"start": v(107, 6.5) * mm, "end": v(109.1, 6.5) * mm, "construction": true});
            skLineSegment(sketch, "E21.0.1.0", {"start": v(107, 19.5) * mm, "end": v(116.4, 19.5) * mm});
            skLineSegment(sketch, "E21.0.1.1", {"start": v(107, 11.5) * mm, "end": v(107, 19.5) * mm});
            skLineSegment(sketch, "E21.0.1.2", {"start": v(107, 11.5) * mm, "end": v(116.4, 11.5) * mm});
            skLineSegment(sketch, "E21.0.1.3", {"start": v(116.4, 11.5) * mm, "end": v(116.4, 19.5) * mm});
            skLineSegment(sketch, "E21.0.1.4", {"start": v(81.4, 11.5) * mm, "end": v(81.4, 19.5) * mm});
            skLineSegment(sketch, "E21.0.1.5", {"start": v(72, 19.5) * mm, "end": v(81.4, 19.5) * mm});
            skLineSegment(sketch, "E21.0.1.6", {"start": v(72, 11.5) * mm, "end": v(72, 19.5) * mm});
            skLineSegment(sketch, "E21.0.1.7", {"start": v(72, 11.5) * mm, "end": v(81.4, 11.5) * mm});
            skLineSegment(sketch, "E21.0.1.8", {"start": v(37, 19.5) * mm, "end": v(46.4, 19.5) * mm});
            skLineSegment(sketch, "E21.0.1.9", {"start": v(37, 11.5) * mm, "end": v(37, 19.5) * mm});
            skLineSegment(sketch, "E21.0.1.10", {"start": v(37, 11.5) * mm, "end": v(46.4, 11.5) * mm});
            skLineSegment(sketch, "E21.0.1.11", {"start": v(46.4, 11.5) * mm, "end": v(46.4, 19.5) * mm});
            skLineSegment(sketch, "E21.0.1.12", {"start": v(2, 19.5) * mm, "end": v(11.4, 19.5) * mm});
            skLineSegment(sketch, "E21.0.1.13", {"start": v(2, 11.5) * mm, "end": v(2, 19.5) * mm});
            skLineSegment(sketch, "E21.0.1.14", {"start": v(2, 11.5) * mm, "end": v(11.4, 11.5) * mm});
            skLineSegment(sketch, "E21.0.1.15", {"start": v(11.4, 11.5) * mm, "end": v(11.4, 19.5) * mm});
            skLineSegment(sketch, "E21.0.2.0", {"start": v(107, 28.5) * mm, "end": v(116.4, 28.5) * mm});
            skLineSegment(sketch, "E21.0.2.1", {"start": v(107, 20.5) * mm, "end": v(107, 28.5) * mm});
            skLineSegment(sketch, "E21.0.2.2", {"start": v(107, 20.5) * mm, "end": v(116.4, 20.5) * mm});
            skLineSegment(sketch, "E21.0.2.3", {"start": v(116.4, 20.5) * mm, "end": v(116.4, 28.5) * mm});
            skLineSegment(sketch, "E21.0.2.4", {"start": v(81.4, 20.5) * mm, "end": v(81.4, 28.5) * mm});
            skLineSegment(sketch, "E21.0.2.5", {"start": v(72, 28.5) * mm, "end": v(81.4, 28.5) * mm});
            skLineSegment(sketch, "E21.0.2.6", {"start": v(72, 20.5) * mm, "end": v(72, 28.5) * mm});
            skLineSegment(sketch, "E21.0.2.7", {"start": v(72, 20.5) * mm, "end": v(81.4, 20.5) * mm});
            skLineSegment(sketch, "E21.0.2.8", {"start": v(37, 28.5) * mm, "end": v(46.4, 28.5) * mm});
            skLineSegment(sketch, "E21.0.2.9", {"start": v(37, 20.5) * mm, "end": v(37, 28.5) * mm});
            skLineSegment(sketch, "E21.0.2.10", {"start": v(37, 20.5) * mm, "end": v(46.4, 20.5) * mm});
            skLineSegment(sketch, "E21.0.2.11", {"start": v(46.4, 20.5) * mm, "end": v(46.4, 28.5) * mm});
            skLineSegment(sketch, "E21.0.2.12", {"start": v(2, 28.5) * mm, "end": v(11.4, 28.5) * mm});
            skLineSegment(sketch, "E21.0.2.13", {"start": v(2, 20.5) * mm, "end": v(2, 28.5) * mm});
            skLineSegment(sketch, "E21.0.2.14", {"start": v(2, 20.5) * mm, "end": v(11.4, 20.5) * mm});
            skLineSegment(sketch, "E21.0.2.15", {"start": v(11.4, 20.5) * mm, "end": v(11.4, 28.5) * mm});
            skLineSegment(sketch, "E21.0.3.0", {"start": v(107, 37.5) * mm, "end": v(116.4, 37.5) * mm});
            skLineSegment(sketch, "E21.0.3.1", {"start": v(107, 29.5) * mm, "end": v(107, 37.5) * mm});
            skLineSegment(sketch, "E21.0.3.2", {"start": v(107, 29.5) * mm, "end": v(116.4, 29.5) * mm});
            skLineSegment(sketch, "E21.0.3.3", {"start": v(116.4, 29.5) * mm, "end": v(116.4, 37.5) * mm});
            skLineSegment(sketch, "E21.0.3.4", {"start": v(81.4, 29.5) * mm, "end": v(81.4, 37.5) * mm});
            skLineSegment(sketch, "E21.0.3.5", {"start": v(72, 37.5) * mm, "end": v(81.4, 37.5) * mm});
            skLineSegment(sketch, "E21.0.3.6", {"start": v(72, 29.5) * mm, "end": v(72, 37.5) * mm});
            skLineSegment(sketch, "E21.0.3.7", {"start": v(72, 29.5) * mm, "end": v(81.4, 29.5) * mm});
            skLineSegment(sketch, "E21.0.3.8", {"start": v(37, 37.5) * mm, "end": v(46.4, 37.5) * mm});
            skLineSegment(sketch, "E21.0.3.9", {"start": v(37, 29.5) * mm, "end": v(37, 37.5) * mm});
            skLineSegment(sketch, "E21.0.3.10", {"start": v(37, 29.5) * mm, "end": v(46.4, 29.5) * mm});
            skLineSegment(sketch, "E21.0.3.11", {"start": v(46.4, 29.5) * mm, "end": v(46.4, 37.5) * mm});
            skLineSegment(sketch, "E21.0.3.12", {"start": v(2, 37.5) * mm, "end": v(11.4, 37.5) * mm});
            skLineSegment(sketch, "E21.0.3.13", {"start": v(2, 29.5) * mm, "end": v(2, 37.5) * mm});
            skLineSegment(sketch, "E21.0.3.14", {"start": v(2, 29.5) * mm, "end": v(11.4, 29.5) * mm});
            skLineSegment(sketch, "E21.0.3.15", {"start": v(11.4, 29.5) * mm, "end": v(11.4, 37.5) * mm});
            skLineSegment(sketch, "E21.0.4.0", {"start": v(107, 46.5) * mm, "end": v(116.4, 46.5) * mm});
            skLineSegment(sketch, "E21.0.4.1", {"start": v(107, 38.5) * mm, "end": v(107, 46.5) * mm});
            skLineSegment(sketch, "E21.0.4.2", {"start": v(107, 38.5) * mm, "end": v(116.4, 38.5) * mm});
            skLineSegment(sketch, "E21.0.4.3", {"start": v(116.4, 38.5) * mm, "end": v(116.4, 46.5) * mm});
            skLineSegment(sketch, "E21.0.4.4", {"start": v(81.4, 38.5) * mm, "end": v(81.4, 46.5) * mm});
            skLineSegment(sketch, "E21.0.4.5", {"start": v(72, 46.5) * mm, "end": v(81.4, 46.5) * mm});
            skLineSegment(sketch, "E21.0.4.6", {"start": v(72, 38.5) * mm, "end": v(72, 46.5) * mm});
            skLineSegment(sketch, "E21.0.4.7", {"start": v(72, 38.5) * mm, "end": v(81.4, 38.5) * mm});
            skLineSegment(sketch, "E21.0.4.8", {"start": v(37, 46.5) * mm, "end": v(46.4, 46.5) * mm});
            skLineSegment(sketch, "E21.0.4.9", {"start": v(37, 38.5) * mm, "end": v(37, 46.5) * mm});
            skLineSegment(sketch, "E21.0.4.10", {"start": v(37, 38.5) * mm, "end": v(46.4, 38.5) * mm});
            skLineSegment(sketch, "E21.0.4.11", {"start": v(46.4, 38.5) * mm, "end": v(46.4, 46.5) * mm});
            skLineSegment(sketch, "E21.0.4.12", {"start": v(2, 46.5) * mm, "end": v(11.4, 46.5) * mm});
            skLineSegment(sketch, "E21.0.4.13", {"start": v(2, 38.5) * mm, "end": v(2, 46.5) * mm});
            skLineSegment(sketch, "E21.0.4.14", {"start": v(2, 38.5) * mm, "end": v(11.4, 38.5) * mm});
            skLineSegment(sketch, "E21.0.4.15", {"start": v(11.4, 38.5) * mm, "end": v(11.4, 46.5) * mm});
            skLineSegment(sketch, "E21.1.0.0", {"start": v(117.4, 10.5) * mm, "end": v(126.8, 10.5) * mm});
            skLineSegment(sketch, "E21.1.0.1", {"start": v(117.4, 2.5) * mm, "end": v(117.4, 10.5) * mm});
            skLineSegment(sketch, "E21.1.0.2", {"start": v(117.4, 2.5) * mm, "end": v(126.8, 2.5) * mm});
            skLineSegment(sketch, "E21.1.0.3", {"start": v(126.8, 2.5) * mm, "end": v(126.8, 10.5) * mm});
            skLineSegment(sketch, "E21.1.0.4", {"start": v(91.8, 2.5) * mm, "end": v(91.8, 10.5) * mm});
            skLineSegment(sketch, "E21.1.0.5", {"start": v(82.4, 10.5) * mm, "end": v(91.8, 10.5) * mm});
            skLineSegment(sketch, "E21.1.0.6", {"start": v(82.4, 2.5) * mm, "end": v(82.4, 10.5) * mm});
            skLineSegment(sketch, "E21.1.0.7", {"start": v(82.4, 2.5) * mm, "end": v(91.8, 2.5) * mm});
            skLineSegment(sketch, "E21.1.0.8", {"start": v(47.4, 10.5) * mm, "end": v(56.8, 10.5) * mm});
            skLineSegment(sketch, "E21.1.0.9", {"start": v(47.4, 2.5) * mm, "end": v(47.4, 10.5) * mm});
            skLineSegment(sketch, "E21.1.0.10", {"start": v(47.4, 2.5) * mm, "end": v(56.8, 2.5) * mm});
            skLineSegment(sketch, "E21.1.0.11", {"start": v(56.8, 2.5) * mm, "end": v(56.8, 10.5) * mm});
            skLineSegment(sketch, "E21.1.0.12", {"start": v(12.4, 10.5) * mm, "end": v(21.8, 10.5) * mm});
            skLineSegment(sketch, "E21.1.0.13", {"start": v(12.4, 2.5) * mm, "end": v(12.4, 10.5) * mm});
            skLineSegment(sketch, "E21.1.0.14", {"start": v(12.4, 2.5) * mm, "end": v(21.8, 2.5) * mm});
            skLineSegment(sketch, "E21.1.0.15", {"start": v(21.8, 2.5) * mm, "end": v(21.8, 10.5) * mm});
            skLineSegment(sketch, "E21.1.1.0", {"start": v(117.4, 19.5) * mm, "end": v(126.8, 19.5) * mm});
            skLineSegment(sketch, "E21.1.1.1", {"start": v(117.4, 11.5) * mm, "end": v(117.4, 19.5) * mm});
            skLineSegment(sketch, "E21.1.1.2", {"start": v(117.4, 11.5) * mm, "end": v(126.8, 11.5) * mm});
            skLineSegment(sketch, "E21.1.1.3", {"start": v(126.8, 11.5) * mm, "end": v(126.8, 19.5) * mm});
            skLineSegment(sketch, "E21.1.1.4", {"start": v(91.8, 11.5) * mm, "end": v(91.8, 19.5) * mm});
            skLineSegment(sketch, "E21.1.1.5", {"start": v(82.4, 19.5) * mm, "end": v(91.8, 19.5) * mm});
            skLineSegment(sketch, "E21.1.1.6", {"start": v(82.4, 11.5) * mm, "end": v(82.4, 19.5) * mm});
            skLineSegment(sketch, "E21.1.1.7", {"start": v(82.4, 11.5) * mm, "end": v(91.8, 11.5) * mm});
            skLineSegment(sketch, "E21.1.1.8", {"start": v(47.4, 19.5) * mm, "end": v(56.8, 19.5) * mm});
            skLineSegment(sketch, "E21.1.1.9", {"start": v(47.4, 11.5) * mm, "end": v(47.4, 19.5) * mm});
            skLineSegment(sketch, "E21.1.1.10", {"start": v(47.4, 11.5) * mm, "end": v(56.8, 11.5) * mm});
            skLineSegment(sketch, "E21.1.1.11", {"start": v(56.8, 11.5) * mm, "end": v(56.8, 19.5) * mm});
            skLineSegment(sketch, "E21.1.1.12", {"start": v(12.4, 19.5) * mm, "end": v(21.8, 19.5) * mm});
            skLineSegment(sketch, "E21.1.1.13", {"start": v(12.4, 11.5) * mm, "end": v(12.4, 19.5) * mm});
            skLineSegment(sketch, "E21.1.1.14", {"start": v(12.4, 11.5) * mm, "end": v(21.8, 11.5) * mm});
            skLineSegment(sketch, "E21.1.1.15", {"start": v(21.8, 11.5) * mm, "end": v(21.8, 19.5) * mm});
            skLineSegment(sketch, "E21.1.2.0", {"start": v(117.4, 28.5) * mm, "end": v(126.8, 28.5) * mm});
            skLineSegment(sketch, "E21.1.2.1", {"start": v(117.4, 20.5) * mm, "end": v(117.4, 28.5) * mm});
            skLineSegment(sketch, "E21.1.2.2", {"start": v(117.4, 20.5) * mm, "end": v(126.8, 20.5) * mm});
            skLineSegment(sketch, "E21.1.2.3", {"start": v(126.8, 20.5) * mm, "end": v(126.8, 28.5) * mm});
            skLineSegment(sketch, "E21.1.2.4", {"start": v(91.8, 20.5) * mm, "end": v(91.8, 28.5) * mm});
            skLineSegment(sketch, "E21.1.2.5", {"start": v(82.4, 28.5) * mm, "end": v(91.8, 28.5) * mm});
            skLineSegment(sketch, "E21.1.2.6", {"start": v(82.4, 20.5) * mm, "end": v(82.4, 28.5) * mm});
            skLineSegment(sketch, "E21.1.2.7", {"start": v(82.4, 20.5) * mm, "end": v(91.8, 20.5) * mm});
            skLineSegment(sketch, "E21.1.2.8", {"start": v(47.4, 28.5) * mm, "end": v(56.8, 28.5) * mm});
            skLineSegment(sketch, "E21.1.2.9", {"start": v(47.4, 20.5) * mm, "end": v(47.4, 28.5) * mm});
            skLineSegment(sketch, "E21.1.2.10", {"start": v(47.4, 20.5) * mm, "end": v(56.8, 20.5) * mm});
            skLineSegment(sketch, "E21.1.2.11", {"start": v(56.8, 20.5) * mm, "end": v(56.8, 28.5) * mm});
            skLineSegment(sketch, "E21.1.2.12", {"start": v(12.4, 28.5) * mm, "end": v(21.8, 28.5) * mm});
            skLineSegment(sketch, "E21.1.2.13", {"start": v(12.4, 20.5) * mm, "end": v(12.4, 28.5) * mm});
            skLineSegment(sketch, "E21.1.2.14", {"start": v(12.4, 20.5) * mm, "end": v(21.8, 20.5) * mm});
            skLineSegment(sketch, "E21.1.2.15", {"start": v(21.8, 20.5) * mm, "end": v(21.8, 28.5) * mm});
            skLineSegment(sketch, "E21.1.3.0", {"start": v(117.4, 37.5) * mm, "end": v(126.8, 37.5) * mm});
            skLineSegment(sketch, "E21.1.3.1", {"start": v(117.4, 29.5) * mm, "end": v(117.4, 37.5) * mm});
            skLineSegment(sketch, "E21.1.3.2", {"start": v(117.4, 29.5) * mm, "end": v(126.8, 29.5) * mm});
            skLineSegment(sketch, "E21.1.3.3", {"start": v(126.8, 29.5) * mm, "end": v(126.8, 37.5) * mm});
            skLineSegment(sketch, "E21.1.3.4", {"start": v(91.8, 29.5) * mm, "end": v(91.8, 37.5) * mm});
            skLineSegment(sketch, "E21.1.3.5", {"start": v(82.4, 37.5) * mm, "end": v(91.8, 37.5) * mm});
            skLineSegment(sketch, "E21.1.3.6", {"start": v(82.4, 29.5) * mm, "end": v(82.4, 37.5) * mm});
            skLineSegment(sketch, "E21.1.3.7", {"start": v(82.4, 29.5) * mm, "end": v(91.8, 29.5) * mm});
            skLineSegment(sketch, "E21.1.3.8", {"start": v(47.4, 37.5) * mm, "end": v(56.8, 37.5) * mm});
            skLineSegment(sketch, "E21.1.3.9", {"start": v(47.4, 29.5) * mm, "end": v(47.4, 37.5) * mm});
            skLineSegment(sketch, "E21.1.3.10", {"start": v(47.4, 29.5) * mm, "end": v(56.8, 29.5) * mm});
            skLineSegment(sketch, "E21.1.3.11", {"start": v(56.8, 29.5) * mm, "end": v(56.8, 37.5) * mm});
            skLineSegment(sketch, "E21.1.3.12", {"start": v(12.4, 37.5) * mm, "end": v(21.8, 37.5) * mm});
            skLineSegment(sketch, "E21.1.3.13", {"start": v(12.4, 29.5) * mm, "end": v(12.4, 37.5) * mm});
            skLineSegment(sketch, "E21.1.3.14", {"start": v(12.4, 29.5) * mm, "end": v(21.8, 29.5) * mm});
            skLineSegment(sketch, "E21.1.3.15", {"start": v(21.8, 29.5) * mm, "end": v(21.8, 37.5) * mm});
            skLineSegment(sketch, "E21.1.4.0", {"start": v(117.4, 46.5) * mm, "end": v(126.8, 46.5) * mm});
            skLineSegment(sketch, "E21.1.4.1", {"start": v(117.4, 38.5) * mm, "end": v(117.4, 46.5) * mm});
            skLineSegment(sketch, "E21.1.4.2", {"start": v(117.4, 38.5) * mm, "end": v(126.8, 38.5) * mm});
            skLineSegment(sketch, "E21.1.4.3", {"start": v(126.8, 38.5) * mm, "end": v(126.8, 46.5) * mm});
            skLineSegment(sketch, "E21.1.4.4", {"start": v(91.8, 38.5) * mm, "end": v(91.8, 46.5) * mm});
            skLineSegment(sketch, "E21.1.4.5", {"start": v(82.4, 46.5) * mm, "end": v(91.8, 46.5) * mm});
            skLineSegment(sketch, "E21.1.4.6", {"start": v(82.4, 38.5) * mm, "end": v(82.4, 46.5) * mm});
            skLineSegment(sketch, "E21.1.4.7", {"start": v(82.4, 38.5) * mm, "end": v(91.8, 38.5) * mm});
            skLineSegment(sketch, "E21.1.4.8", {"start": v(47.4, 46.5) * mm, "end": v(56.8, 46.5) * mm});
            skLineSegment(sketch, "E21.1.4.9", {"start": v(47.4, 38.5) * mm, "end": v(47.4, 46.5) * mm});
            skLineSegment(sketch, "E21.1.4.10", {"start": v(47.4, 38.5) * mm, "end": v(56.8, 38.5) * mm});
            skLineSegment(sketch, "E21.1.4.11", {"start": v(56.8, 38.5) * mm, "end": v(56.8, 46.5) * mm});
            skLineSegment(sketch, "E21.1.4.12", {"start": v(12.4, 46.5) * mm, "end": v(21.8, 46.5) * mm});
            skLineSegment(sketch, "E21.1.4.13", {"start": v(12.4, 38.5) * mm, "end": v(12.4, 46.5) * mm});
            skLineSegment(sketch, "E21.1.4.14", {"start": v(12.4, 38.5) * mm, "end": v(21.8, 38.5) * mm});
            skLineSegment(sketch, "E21.1.4.15", {"start": v(21.8, 38.5) * mm, "end": v(21.8, 46.5) * mm});
            skLineSegment(sketch, "E21.2.0.0", {"start": v(127.8, 10.5) * mm, "end": v(137.2, 10.5) * mm});
            skLineSegment(sketch, "E21.2.0.1", {"start": v(127.8, 2.5) * mm, "end": v(127.8, 10.5) * mm});
            skLineSegment(sketch, "E21.2.0.2", {"start": v(127.8, 2.5) * mm, "end": v(137.2, 2.5) * mm});
            skLineSegment(sketch, "E21.2.0.3", {"start": v(137.2, 2.5) * mm, "end": v(137.2, 10.5) * mm});
            skLineSegment(sketch, "E21.2.0.4", {"start": v(102.2, 2.5) * mm, "end": v(102.2, 10.5) * mm});
            skLineSegment(sketch, "E21.2.0.5", {"start": v(92.8, 10.5) * mm, "end": v(102.2, 10.5) * mm});
            skLineSegment(sketch, "E21.2.0.6", {"start": v(92.8, 2.5) * mm, "end": v(92.8, 10.5) * mm});
            skLineSegment(sketch, "E21.2.0.7", {"start": v(92.8, 2.5) * mm, "end": v(102.2, 2.5) * mm});
            skLineSegment(sketch, "E21.2.0.8", {"start": v(57.8, 10.5) * mm, "end": v(67.2, 10.5) * mm});
            skLineSegment(sketch, "E21.2.0.9", {"start": v(57.8, 2.5) * mm, "end": v(57.8, 10.5) * mm});
            skLineSegment(sketch, "E21.2.0.10", {"start": v(57.8, 2.5) * mm, "end": v(67.2, 2.5) * mm});
            skLineSegment(sketch, "E21.2.0.11", {"start": v(67.2, 2.5) * mm, "end": v(67.2, 10.5) * mm});
            skLineSegment(sketch, "E21.2.0.12", {"start": v(22.8, 10.5) * mm, "end": v(32.2, 10.5) * mm});
            skLineSegment(sketch, "E21.2.0.13", {"start": v(22.8, 2.5) * mm, "end": v(22.8, 10.5) * mm});
            skLineSegment(sketch, "E21.2.0.14", {"start": v(22.8, 2.5) * mm, "end": v(32.2, 2.5) * mm});
            skLineSegment(sketch, "E21.2.0.15", {"start": v(32.2, 2.5) * mm, "end": v(32.2, 10.5) * mm});
            skLineSegment(sketch, "E21.2.1.0", {"start": v(127.8, 19.5) * mm, "end": v(137.2, 19.5) * mm});
            skLineSegment(sketch, "E21.2.1.1", {"start": v(127.8, 11.5) * mm, "end": v(127.8, 19.5) * mm});
            skLineSegment(sketch, "E21.2.1.2", {"start": v(127.8, 11.5) * mm, "end": v(137.2, 11.5) * mm});
            skLineSegment(sketch, "E21.2.1.3", {"start": v(137.2, 11.5) * mm, "end": v(137.2, 19.5) * mm});
            skLineSegment(sketch, "E21.2.1.4", {"start": v(102.2, 11.5) * mm, "end": v(102.2, 19.5) * mm});
            skLineSegment(sketch, "E21.2.1.5", {"start": v(92.8, 19.5) * mm, "end": v(102.2, 19.5) * mm});
            skLineSegment(sketch, "E21.2.1.6", {"start": v(92.8, 11.5) * mm, "end": v(92.8, 19.5) * mm});
            skLineSegment(sketch, "E21.2.1.7", {"start": v(92.8, 11.5) * mm, "end": v(102.2, 11.5) * mm});
            skLineSegment(sketch, "E21.2.1.8", {"start": v(57.8, 19.5) * mm, "end": v(67.2, 19.5) * mm});
            skLineSegment(sketch, "E21.2.1.9", {"start": v(57.8, 11.5) * mm, "end": v(57.8, 19.5) * mm});
            skLineSegment(sketch, "E21.2.1.10", {"start": v(57.8, 11.5) * mm, "end": v(67.2, 11.5) * mm});
            skLineSegment(sketch, "E21.2.1.11", {"start": v(67.2, 11.5) * mm, "end": v(67.2, 19.5) * mm});
            skLineSegment(sketch, "E21.2.1.12", {"start": v(22.8, 19.5) * mm, "end": v(32.2, 19.5) * mm});
            skLineSegment(sketch, "E21.2.1.13", {"start": v(22.8, 11.5) * mm, "end": v(22.8, 19.5) * mm});
            skLineSegment(sketch, "E21.2.1.14", {"start": v(22.8, 11.5) * mm, "end": v(32.2, 11.5) * mm});
            skLineSegment(sketch, "E21.2.1.15", {"start": v(32.2, 11.5) * mm, "end": v(32.2, 19.5) * mm});
            skLineSegment(sketch, "E21.2.2.0", {"start": v(127.8, 28.5) * mm, "end": v(137.2, 28.5) * mm});
            skLineSegment(sketch, "E21.2.2.1", {"start": v(127.8, 20.5) * mm, "end": v(127.8, 28.5) * mm});
            skLineSegment(sketch, "E21.2.2.2", {"start": v(127.8, 20.5) * mm, "end": v(137.2, 20.5) * mm});
            skLineSegment(sketch, "E21.2.2.3", {"start": v(137.2, 20.5) * mm, "end": v(137.2, 28.5) * mm});
            skLineSegment(sketch, "E21.2.2.4", {"start": v(102.2, 20.5) * mm, "end": v(102.2, 28.5) * mm});
            skLineSegment(sketch, "E21.2.2.5", {"start": v(92.8, 28.5) * mm, "end": v(102.2, 28.5) * mm});
            skLineSegment(sketch, "E21.2.2.6", {"start": v(92.8, 20.5) * mm, "end": v(92.8, 28.5) * mm});
            skLineSegment(sketch, "E21.2.2.7", {"start": v(92.8, 20.5) * mm, "end": v(102.2, 20.5) * mm});
            skLineSegment(sketch, "E21.2.2.8", {"start": v(57.8, 28.5) * mm, "end": v(67.2, 28.5) * mm});
            skLineSegment(sketch, "E21.2.2.9", {"start": v(57.8, 20.5) * mm, "end": v(57.8, 28.5) * mm});
            skLineSegment(sketch, "E21.2.2.10", {"start": v(57.8, 20.5) * mm, "end": v(67.2, 20.5) * mm});
            skLineSegment(sketch, "E21.2.2.11", {"start": v(67.2, 20.5) * mm, "end": v(67.2, 28.5) * mm});
            skLineSegment(sketch, "E21.2.2.12", {"start": v(22.8, 28.5) * mm, "end": v(32.2, 28.5) * mm});
            skLineSegment(sketch, "E21.2.2.13", {"start": v(22.8, 20.5) * mm, "end": v(22.8, 28.5) * mm});
            skLineSegment(sketch, "E21.2.2.14", {"start": v(22.8, 20.5) * mm, "end": v(32.2, 20.5) * mm});
            skLineSegment(sketch, "E21.2.2.15", {"start": v(32.2, 20.5) * mm, "end": v(32.2, 28.5) * mm});
            skLineSegment(sketch, "E21.2.3.0", {"start": v(127.8, 37.5) * mm, "end": v(137.2, 37.5) * mm});
            skLineSegment(sketch, "E21.2.3.1", {"start": v(127.8, 29.5) * mm, "end": v(127.8, 37.5) * mm});
            skLineSegment(sketch, "E21.2.3.2", {"start": v(127.8, 29.5) * mm, "end": v(137.2, 29.5) * mm});
            skLineSegment(sketch, "E21.2.3.3", {"start": v(137.2, 29.5) * mm, "end": v(137.2, 37.5) * mm});
            skLineSegment(sketch, "E21.2.3.4", {"start": v(102.2, 29.5) * mm, "end": v(102.2, 37.5) * mm});
            skLineSegment(sketch, "E21.2.3.5", {"start": v(92.8, 37.5) * mm, "end": v(102.2, 37.5) * mm});
            skLineSegment(sketch, "E21.2.3.6", {"start": v(92.8, 29.5) * mm, "end": v(92.8, 37.5) * mm});
            skLineSegment(sketch, "E21.2.3.7", {"start": v(92.8, 29.5) * mm, "end": v(102.2, 29.5) * mm});
            skLineSegment(sketch, "E21.2.3.8", {"start": v(57.8, 37.5) * mm, "end": v(67.2, 37.5) * mm});
            skLineSegment(sketch, "E21.2.3.9", {"start": v(57.8, 29.5) * mm, "end": v(57.8, 37.5) * mm});
            skLineSegment(sketch, "E21.2.3.10", {"start": v(57.8, 29.5) * mm, "end": v(67.2, 29.5) * mm});
            skLineSegment(sketch, "E21.2.3.11", {"start": v(67.2, 29.5) * mm, "end": v(67.2, 37.5) * mm});
            skLineSegment(sketch, "E21.2.3.12", {"start": v(22.8, 37.5) * mm, "end": v(32.2, 37.5) * mm});
            skLineSegment(sketch, "E21.2.3.13", {"start": v(22.8, 29.5) * mm, "end": v(22.8, 37.5) * mm});
            skLineSegment(sketch, "E21.2.3.14", {"start": v(22.8, 29.5) * mm, "end": v(32.2, 29.5) * mm});
            skLineSegment(sketch, "E21.2.3.15", {"start": v(32.2, 29.5) * mm, "end": v(32.2, 37.5) * mm});
            skLineSegment(sketch, "E21.2.4.0", {"start": v(127.8, 46.5) * mm, "end": v(137.2, 46.5) * mm});
            skLineSegment(sketch, "E21.2.4.1", {"start": v(127.8, 38.5) * mm, "end": v(127.8, 46.5) * mm});
            skLineSegment(sketch, "E21.2.4.2", {"start": v(127.8, 38.5) * mm, "end": v(137.2, 38.5) * mm});
            skLineSegment(sketch, "E21.2.4.3", {"start": v(137.2, 38.5) * mm, "end": v(137.2, 46.5) * mm});
            skLineSegment(sketch, "E21.2.4.4", {"start": v(102.2, 38.5) * mm, "end": v(102.2, 46.5) * mm});
            skLineSegment(sketch, "E21.2.4.5", {"start": v(92.8, 46.5) * mm, "end": v(102.2, 46.5) * mm});
            skLineSegment(sketch, "E21.2.4.6", {"start": v(92.8, 38.5) * mm, "end": v(92.8, 46.5) * mm});
            skLineSegment(sketch, "E21.2.4.7", {"start": v(92.8, 38.5) * mm, "end": v(102.2, 38.5) * mm});
            skLineSegment(sketch, "E21.2.4.8", {"start": v(57.8, 46.5) * mm, "end": v(67.2, 46.5) * mm});
            skLineSegment(sketch, "E21.2.4.9", {"start": v(57.8, 38.5) * mm, "end": v(57.8, 46.5) * mm});
            skLineSegment(sketch, "E21.2.4.10", {"start": v(57.8, 38.5) * mm, "end": v(67.2, 38.5) * mm});
            skLineSegment(sketch, "E21.2.4.11", {"start": v(67.2, 38.5) * mm, "end": v(67.2, 46.5) * mm});
            skLineSegment(sketch, "E21.2.4.12", {"start": v(22.8, 46.5) * mm, "end": v(32.2, 46.5) * mm});
            skLineSegment(sketch, "E21.2.4.13", {"start": v(22.8, 38.5) * mm, "end": v(22.8, 46.5) * mm});
            skLineSegment(sketch, "E21.2.4.14", {"start": v(22.8, 38.5) * mm, "end": v(32.2, 38.5) * mm});
            skLineSegment(sketch, "E21.2.4.15", {"start": v(32.2, 38.5) * mm, "end": v(32.2, 46.5) * mm});
            skLineSegment(sketch, "E21.direction1", {"start": v(2, 2.5) * mm, "end": v(12.4, 2.5) * mm, "construction": true});
            skLineSegment(sketch, "E21.direction2", {"start": v(2, 2.5) * mm, "end": v(2, 11.5) * mm, "construction": true});
            skLineSegment(sketch, "E22", {"start": v(0, 24.5) * mm, "end": v(-14, 24.5) * mm, "construction": true});
            skSolve(sketch);
        }
        {
            var Q0;
            Q0=qSketchRegion(id+"F2",true);
            extrude(context, id + "F3", {"entities" : qUnion([Q0]), "depth" : 3 * mm, "offsetDistance" : 25 * mm});
        }
        {
            var Q0;
            Q0=makeQuery(id+"F3.opExtrude","CAP_FACE",FACE,{"disambiguationData":[OSD([sQuery(id+"F2.wireOp",EDGE,"E7.bottom"),sQuery(id+"F2.wireOp",EDGE,"E7.top"),sQuery(id+"F2.wireOp",EDGE,"E7.left"),sQuery(id+"F2.wireOp",EDGE,"E7.right"),sQuery(id+"F2.wireOp",EDGE,"E9.bottom"),sQuery(id+"F2.wireOp",EDGE,"E9.top"),sQuery(id+"F2.wireOp",EDGE,"E9.left"),sQuery(id+"F2.wireOp",EDGE,"E9.right"),sQuery(id+"F2.wireOp",EDGE,"E10.bottom"),sQuery(id+"F2.wireOp",EDGE,"E10.top"),sQuery(id+"F2.wireOp",EDGE,"E10.left"),sQuery(id+"F2.wireOp",EDGE,"E10.right"),sQuery(id+"F2.wireOp",EDGE,"E15.bottom"),sQuery(id+"F2.wireOp",EDGE,"E15.top"),sQuery(id+"F2.wireOp",EDGE,"E15.left"),sQuery(id+"F2.wireOp",EDGE,"E15.right"),sQuery(id+"F2.wireOp",EDGE,"E16.bottom"),sQuery(id+"F2.wireOp",EDGE,"E16.top"),sQuery(id+"F2.wireOp",EDGE,"E16.left"),sQuery(id+"F2.wireOp",EDGE,"E16.right"),sQuery(id+"F2.wireOp",EDGE,"E21.0.1.0"),sQuery(id+"F2.wireOp",EDGE,"E21.0.1.1"),sQuery(id+"F2.wireOp",EDGE,"E21.0.1.2"),sQuery(id+"F2.wireOp",EDGE,"E21.0.1.3"),sQuery(id+"F2.wireOp",EDGE,"E21.0.1.4"),sQuery(id+"F2.wireOp",EDGE,"E21.0.1.5"),sQuery(id+"F2.wireOp",EDGE,"E21.0.1.6"),sQuery(id+"F2.wireOp",EDGE,"E21.0.1.7"),sQuery(id+"F2.wireOp",EDGE,"E21.0.1.8"),sQuery(id+"F2.wireOp",EDGE,"E21.0.1.9"),sQuery(id+"F2.wireOp",EDGE,"E21.0.1.10"),sQuery(id+"F2.wireOp",EDGE,"E21.0.1.11"),sQuery(id+"F2.wireOp",EDGE,"E21.0.1.12"),sQuery(id+"F2.wireOp",EDGE,"E21.0.1.13"),sQuery(id+"F2.wireOp",EDGE,"E21.0.1.14"),sQuery(id+"F2.wireOp",EDGE,"E21.0.1.15"),sQuery(id+"F2.wireOp",EDGE,"E21.0.2.0"),sQuery(id+"F2.wireOp",EDGE,"E21.0.2.1"),sQuery(id+"F2.wireOp",EDGE,"E21.0.2.2"),sQuery(id+"F2.wireOp",EDGE,"E21.0.2.3"),sQuery(id+"F2.wireOp",EDGE,"E21.0.2.4"),sQuery(id+"F2.wireOp",EDGE,"E21.0.2.5"),sQuery(id+"F2.wireOp",EDGE,"E21.0.2.6"),sQuery(id+"F2.wireOp",EDGE,"E21.0.2.7"),sQuery(id+"F2.wireOp",EDGE,"E21.0.2.8"),sQuery(id+"F2.wireOp",EDGE,"E21.0.2.9"),sQuery(id+"F2.wireOp",EDGE,"E21.0.2.10"),sQuery(id+"F2.wireOp",EDGE,"E21.0.2.11"),sQuery(id+"F2.wireOp",EDGE,"E21.0.2.12"),sQuery(id+"F2.wireOp",EDGE,"E21.0.2.13"),sQuery(id+"F2.wireOp",EDGE,"E21.0.2.14"),sQuery(id+"F2.wireOp",EDGE,"E21.0.2.15"),sQuery(id+"F2.wireOp",EDGE,"E21.0.3.0"),sQuery(id+"F2.wireOp",EDGE,"E21.0.3.1"),sQuery(id+"F2.wireOp",EDGE,"E21.0.3.2"),sQuery(id+"F2.wireOp",EDGE,"E21.0.3.3"),sQuery(id+"F2.wireOp",EDGE,"E21.0.3.4"),sQuery(id+"F2.wireOp",EDGE,"E21.0.3.5"),sQuery(id+"F2.wireOp",EDGE,"E21.0.3.6"),sQuery(id+"F2.wireOp",EDGE,"E21.0.3.7"),sQuery(id+"F2.wireOp",EDGE,"E21.0.3.8"),sQuery(id+"F2.wireOp",EDGE,"E21.0.3.9"),sQuery(id+"F2.wireOp",EDGE,"E21.0.3.10"),sQuery(id+"F2.wireOp",EDGE,"E21.0.3.11"),sQuery(id+"F2.wireOp",EDGE,"E21.0.3.12"),sQuery(id+"F2.wireOp",EDGE,"E21.0.3.13"),sQuery(id+"F2.wireOp",EDGE,"E21.0.3.14"),sQuery(id+"F2.wireOp",EDGE,"E21.0.3.15"),sQuery(id+"F2.wireOp",EDGE,"E21.0.4.0"),sQuery(id+"F2.wireOp",EDGE,"E21.0.4.1"),sQuery(id+"F2.wireOp",EDGE,"E21.0.4.2"),sQuery(id+"F2.wireOp",EDGE,"E21.0.4.3"),sQuery(id+"F2.wireOp",EDGE,"E21.0.4.4"),sQuery(id+"F2.wireOp",EDGE,"E21.0.4.5"),sQuery(id+"F2.wireOp",EDGE,"E21.0.4.6"),sQuery(id+"F2.wireOp",EDGE,"E21.0.4.7"),sQuery(id+"F2.wireOp",EDGE,"E21.0.4.8"),sQuery(id+"F2.wireOp",EDGE,"E21.0.4.9"),sQuery(id+"F2.wireOp",EDGE,"E21.0.4.10"),sQuery(id+"F2.wireOp",EDGE,"E21.0.4.11"),sQuery(id+"F2.wireOp",EDGE,"E21.0.4.12"),sQuery(id+"F2.wireOp",EDGE,"E21.0.4.13"),sQuery(id+"F2.wireOp",EDGE,"E21.0.4.14"),sQuery(id+"F2.wireOp",EDGE,"E21.0.4.15"),sQuery(id+"F2.wireOp",EDGE,"E21.1.0.0"),sQuery(id+"F2.wireOp",EDGE,"E21.1.0.1"),sQuery(id+"F2.wireOp",EDGE,"E21.1.0.2"),sQuery(id+"F2.wireOp",EDGE,"E21.1.0.3"),sQuery(id+"F2.wireOp",EDGE,"E21.1.0.4"),sQuery(id+"F2.wireOp",EDGE,"E21.1.0.5"),sQuery(id+"F2.wireOp",EDGE,"E21.1.0.6"),sQuery(id+"F2.wireOp",EDGE,"E21.1.0.7"),sQuery(id+"F2.wireOp",EDGE,"E21.1.0.8"),sQuery(id+"F2.wireOp",EDGE,"E21.1.0.9"),sQuery(id+"F2.wireOp",EDGE,"E21.1.0.10"),sQuery(id+"F2.wireOp",EDGE,"E21.1.0.11"),sQuery(id+"F2.wireOp",EDGE,"E21.1.0.12"),sQuery(id+"F2.wireOp",EDGE,"E21.1.0.13"),sQuery(id+"F2.wireOp",EDGE,"E21.1.0.14"),sQuery(id+"F2.wireOp",EDGE,"E21.1.0.15"),sQuery(id+"F2.wireOp",EDGE,"E21.1.1.0"),sQuery(id+"F2.wireOp",EDGE,"E21.1.1.1"),sQuery(id+"F2.wireOp",EDGE,"E21.1.1.2"),sQuery(id+"F2.wireOp",EDGE,"E21.1.1.3"),sQuery(id+"F2.wireOp",EDGE,"E21.1.1.4"),sQuery(id+"F2.wireOp",EDGE,"E21.1.1.5"),sQuery(id+"F2.wireOp",EDGE,"E21.1.1.6"),sQuery(id+"F2.wireOp",EDGE,"E21.1.1.7"),sQuery(id+"F2.wireOp",EDGE,"E21.1.1.8"),sQuery(id+"F2.wireOp",EDGE,"E21.1.1.9"),sQuery(id+"F2.wireOp",EDGE,"E21.1.1.10"),sQuery(id+"F2.wireOp",EDGE,"E21.1.1.11"),sQuery(id+"F2.wireOp",EDGE,"E21.1.1.12"),sQuery(id+"F2.wireOp",EDGE,"E21.1.1.13"),sQuery(id+"F2.wireOp",EDGE,"E21.1.1.14"),sQuery(id+"F2.wireOp",EDGE,"E21.1.1.15"),sQuery(id+"F2.wireOp",EDGE,"E21.1.2.0"),sQuery(id+"F2.wireOp",EDGE,"E21.1.2.1"),sQuery(id+"F2.wireOp",EDGE,"E21.1.2.2"),sQuery(id+"F2.wireOp",EDGE,"E21.1.2.3"),sQuery(id+"F2.wireOp",EDGE,"E21.1.2.4"),sQuery(id+"F2.wireOp",EDGE,"E21.1.2.5"),sQuery(id+"F2.wireOp",EDGE,"E21.1.2.6"),sQuery(id+"F2.wireOp",EDGE,"E21.1.2.7"),sQuery(id+"F2.wireOp",EDGE,"E21.1.2.8"),sQuery(id+"F2.wireOp",EDGE,"E21.1.2.9"),sQuery(id+"F2.wireOp",EDGE,"E21.1.2.10"),sQuery(id+"F2.wireOp",EDGE,"E21.1.2.11"),sQuery(id+"F2.wireOp",EDGE,"E21.1.2.12"),sQuery(id+"F2.wireOp",EDGE,"E21.1.2.13"),sQuery(id+"F2.wireOp",EDGE,"E21.1.2.14"),sQuery(id+"F2.wireOp",EDGE,"E21.1.2.15"),sQuery(id+"F2.wireOp",EDGE,"E21.1.3.0"),sQuery(id+"F2.wireOp",EDGE,"E21.1.3.1"),sQuery(id+"F2.wireOp",EDGE,"E21.1.3.2"),sQuery(id+"F2.wireOp",EDGE,"E21.1.3.3"),sQuery(id+"F2.wireOp",EDGE,"E21.1.3.4"),sQuery(id+"F2.wireOp",EDGE,"E21.1.3.5"),sQuery(id+"F2.wireOp",EDGE,"E21.1.3.6"),sQuery(id+"F2.wireOp",EDGE,"E21.1.3.7"),sQuery(id+"F2.wireOp",EDGE,"E21.1.3.8"),sQuery(id+"F2.wireOp",EDGE,"E21.1.3.9"),sQuery(id+"F2.wireOp",EDGE,"E21.1.3.10"),sQuery(id+"F2.wireOp",EDGE,"E21.1.3.11"),sQuery(id+"F2.wireOp",EDGE,"E21.1.3.12"),sQuery(id+"F2.wireOp",EDGE,"E21.1.3.13"),sQuery(id+"F2.wireOp",EDGE,"E21.1.3.14"),sQuery(id+"F2.wireOp",EDGE,"E21.1.3.15"),sQuery(id+"F2.wireOp",EDGE,"E21.1.4.0"),sQuery(id+"F2.wireOp",EDGE,"E21.1.4.1"),sQuery(id+"F2.wireOp",EDGE,"E21.1.4.2"),sQuery(id+"F2.wireOp",EDGE,"E21.1.4.3"),sQuery(id+"F2.wireOp",EDGE,"E21.1.4.4"),sQuery(id+"F2.wireOp",EDGE,"E21.1.4.5"),sQuery(id+"F2.wireOp",EDGE,"E21.1.4.6"),sQuery(id+"F2.wireOp",EDGE,"E21.1.4.7"),sQuery(id+"F2.wireOp",EDGE,"E21.1.4.8"),sQuery(id+"F2.wireOp",EDGE,"E21.1.4.9"),sQuery(id+"F2.wireOp",EDGE,"E21.1.4.10"),sQuery(id+"F2.wireOp",EDGE,"E21.1.4.11"),sQuery(id+"F2.wireOp",EDGE,"E21.1.4.12"),sQuery(id+"F2.wireOp",EDGE,"E21.1.4.13"),sQuery(id+"F2.wireOp",EDGE,"E21.1.4.14"),sQuery(id+"F2.wireOp",EDGE,"E21.1.4.15"),sQuery(id+"F2.wireOp",EDGE,"E21.2.0.0"),sQuery(id+"F2.wireOp",EDGE,"E21.2.0.1"),sQuery(id+"F2.wireOp",EDGE,"E21.2.0.2"),sQuery(id+"F2.wireOp",EDGE,"E21.2.0.3"),sQuery(id+"F2.wireOp",EDGE,"E21.2.0.4"),sQuery(id+"F2.wireOp",EDGE,"E21.2.0.5"),sQuery(id+"F2.wireOp",EDGE,"E21.2.0.6"),sQuery(id+"F2.wireOp",EDGE,"E21.2.0.7"),sQuery(id+"F2.wireOp",EDGE,"E21.2.0.8"),sQuery(id+"F2.wireOp",EDGE,"E21.2.0.9"),sQuery(id+"F2.wireOp",EDGE,"E21.2.0.10"),sQuery(id+"F2.wireOp",EDGE,"E21.2.0.11"),sQuery(id+"F2.wireOp",EDGE,"E21.2.0.12"),sQuery(id+"F2.wireOp",EDGE,"E21.2.0.13"),sQuery(id+"F2.wireOp",EDGE,"E21.2.0.14"),sQuery(id+"F2.wireOp",EDGE,"E21.2.0.15"),sQuery(id+"F2.wireOp",EDGE,"E21.2.1.0"),sQuery(id+"F2.wireOp",EDGE,"E21.2.1.1"),sQuery(id+"F2.wireOp",EDGE,"E21.2.1.2"),sQuery(id+"F2.wireOp",EDGE,"E21.2.1.3"),sQuery(id+"F2.wireOp",EDGE,"E21.2.1.4"),sQuery(id+"F2.wireOp",EDGE,"E21.2.1.5"),sQuery(id+"F2.wireOp",EDGE,"E21.2.1.6"),sQuery(id+"F2.wireOp",EDGE,"E21.2.1.7"),sQuery(id+"F2.wireOp",EDGE,"E21.2.1.8"),sQuery(id+"F2.wireOp",EDGE,"E21.2.1.9"),sQuery(id+"F2.wireOp",EDGE,"E21.2.1.10"),sQuery(id+"F2.wireOp",EDGE,"E21.2.1.11"),sQuery(id+"F2.wireOp",EDGE,"E21.2.1.12"),sQuery(id+"F2.wireOp",EDGE,"E21.2.1.13"),sQuery(id+"F2.wireOp",EDGE,"E21.2.1.14"),sQuery(id+"F2.wireOp",EDGE,"E21.2.1.15"),sQuery(id+"F2.wireOp",EDGE,"E21.2.2.0"),sQuery(id+"F2.wireOp",EDGE,"E21.2.2.1"),sQuery(id+"F2.wireOp",EDGE,"E21.2.2.2"),sQuery(id+"F2.wireOp",EDGE,"E21.2.2.3"),sQuery(id+"F2.wireOp",EDGE,"E21.2.2.4"),sQuery(id+"F2.wireOp",EDGE,"E21.2.2.5"),sQuery(id+"F2.wireOp",EDGE,"E21.2.2.6"),sQuery(id+"F2.wireOp",EDGE,"E21.2.2.7"),sQuery(id+"F2.wireOp",EDGE,"E21.2.2.8"),sQuery(id+"F2.wireOp",EDGE,"E21.2.2.9"),sQuery(id+"F2.wireOp",EDGE,"E21.2.2.10"),sQuery(id+"F2.wireOp",EDGE,"E21.2.2.11"),sQuery(id+"F2.wireOp",EDGE,"E21.2.2.12"),sQuery(id+"F2.wireOp",EDGE,"E21.2.2.13"),sQuery(id+"F2.wireOp",EDGE,"E21.2.2.14"),sQuery(id+"F2.wireOp",EDGE,"E21.2.2.15"),sQuery(id+"F2.wireOp",EDGE,"E21.2.3.0"),sQuery(id+"F2.wireOp",EDGE,"E21.2.3.1"),sQuery(id+"F2.wireOp",EDGE,"E21.2.3.2"),sQuery(id+"F2.wireOp",EDGE,"E21.2.3.3"),sQuery(id+"F2.wireOp",EDGE,"E21.2.3.4"),sQuery(id+"F2.wireOp",EDGE,"E21.2.3.5"),sQuery(id+"F2.wireOp",EDGE,"E21.2.3.6"),sQuery(id+"F2.wireOp",EDGE,"E21.2.3.7"),sQuery(id+"F2.wireOp",EDGE,"E21.2.3.8"),sQuery(id+"F2.wireOp",EDGE,"E21.2.3.9"),sQuery(id+"F2.wireOp",EDGE,"E21.2.3.10"),sQuery(id+"F2.wireOp",EDGE,"E21.2.3.11"),sQuery(id+"F2.wireOp",EDGE,"E21.2.3.12"),sQuery(id+"F2.wireOp",EDGE,"E21.2.3.13"),sQuery(id+"F2.wireOp",EDGE,"E21.2.3.14"),sQuery(id+"F2.wireOp",EDGE,"E21.2.3.15"),sQuery(id+"F2.wireOp",EDGE,"E21.2.4.0"),sQuery(id+"F2.wireOp",EDGE,"E21.2.4.1"),sQuery(id+"F2.wireOp",EDGE,"E21.2.4.2"),sQuery(id+"F2.wireOp",EDGE,"E21.2.4.3"),sQuery(id+"F2.wireOp",EDGE,"E21.2.4.4"),sQuery(id+"F2.wireOp",EDGE,"E21.2.4.5"),sQuery(id+"F2.wireOp",EDGE,"E21.2.4.6"),sQuery(id+"F2.wireOp",EDGE,"E21.2.4.7"),sQuery(id+"F2.wireOp",EDGE,"E21.2.4.8"),sQuery(id+"F2.wireOp",EDGE,"E21.2.4.9"),sQuery(id+"F2.wireOp",EDGE,"E21.2.4.10"),sQuery(id+"F2.wireOp",EDGE,"E21.2.4.11"),sQuery(id+"F2.wireOp",EDGE,"E21.2.4.12"),sQuery(id+"F2.wireOp",EDGE,"E21.2.4.13"),sQuery(id+"F2.wireOp",EDGE,"E21.2.4.14"),sQuery(id+"F2.wireOp",EDGE,"E21.2.4.15")])],"isStart":false});
            var sketch = newSketch(context, id + "F4", { "sketchPlane" : qUnion([Q0])});
            skLineSegment(sketch, "E23.bottom", {"start": v(-7.5, 50) * mm, "end": v(-4.5, 50) * mm});
            skLineSegment(sketch, "E23.top", {"start": v(-7.5, 36) * mm, "end": v(-4.5, 36) * mm});
            skLineSegment(sketch, "E23.left", {"start": v(-7.5, 50) * mm, "end": v(-7.5, 36) * mm});
            skLineSegment(sketch, "E23.right", {"start": v(-4.5, 50) * mm, "end": v(-4.5, 36) * mm});
            skLineSegment(sketch, "E24.bottom", {"start": v(-7.5, 13) * mm, "end": v(-4.5, 13) * mm});
            skLineSegment(sketch, "E24.top", {"start": v(-7.5, -1) * mm, "end": v(-4.5, -1) * mm});
            skLineSegment(sketch, "E24.left", {"start": v(-7.5, 13) * mm, "end": v(-7.5, -1) * mm});
            skLineSegment(sketch, "E24.right", {"start": v(-4.5, 13) * mm, "end": v(-4.5, -1) * mm});
            skLineSegment(sketch, "E25.bottom", {"start": v(143.7, 50) * mm, "end": v(146.7, 50) * mm});
            skLineSegment(sketch, "E25.top", {"start": v(143.7, 36) * mm, "end": v(146.7, 36) * mm});
            skLineSegment(sketch, "E25.left", {"start": v(143.7, 50) * mm, "end": v(143.7, 36) * mm});
            skLineSegment(sketch, "E25.right", {"start": v(146.7, 50) * mm, "end": v(146.7, 36) * mm});
            skLineSegment(sketch, "E26.bottom", {"start": v(-14, 33.5) * mm, "end": v(-10.5, 33.5) * mm});
            skLineSegment(sketch, "E26.top", {"start": v(-14, 15.5) * mm, "end": v(-10.5, 15.5) * mm});
            skLineSegment(sketch, "E26.left", {"start": v(-14, 33.5) * mm, "end": v(-14, 15.5) * mm});
            skLineSegment(sketch, "E26.right", {"start": v(-10.5, 33.5) * mm, "end": v(-10.5, 15.5) * mm});
            skLineSegment(sketch, "E27.bottom", {"start": v(153.2, 33.5) * mm, "end": v(149.7, 33.5) * mm});
            skLineSegment(sketch, "E27.top", {"start": v(153.2, 15.5) * mm, "end": v(149.7, 15.5) * mm});
            skLineSegment(sketch, "E27.left", {"start": v(153.2, 33.5) * mm, "end": v(153.2, 15.5) * mm});
            skLineSegment(sketch, "E27.right", {"start": v(149.7, 33.5) * mm, "end": v(149.7, 15.5) * mm});
            skLineSegment(sketch, "E28", {"start": v(-10.5, 24.5) * mm, "end": v(2, 24.5) * mm, "construction": true});
            skLineSegment(sketch, "E29", {"start": v(-14, 57) * mm, "end": v(-7.5, 50) * mm, "construction": true});
            skLineSegment(sketch, "E30", {"start": v(-7.5, -1) * mm, "end": v(-14, -8) * mm, "construction": true});
            skLineSegment(sketch, "E31.bottom", {"start": v(4.85, 57) * mm, "end": v(22.85, 57) * mm});
            skLineSegment(sketch, "E31.top", {"start": v(4.85, 53.5) * mm, "end": v(22.85, 53.5) * mm});
            skLineSegment(sketch, "E31.left", {"start": v(4.85, 57) * mm, "end": v(4.85, 53.5) * mm});
            skLineSegment(sketch, "E31.right", {"start": v(22.85, 57) * mm, "end": v(22.85, 53.5) * mm});
            skLineSegment(sketch, "E32.bottom", {"start": v(42.02, 57) * mm, "end": v(60.02, 57) * mm});
            skLineSegment(sketch, "E32.top", {"start": v(42.02, 53.5) * mm, "end": v(60.02, 53.5) * mm});
            skLineSegment(sketch, "E32.left", {"start": v(42.02, 57) * mm, "end": v(42.02, 53.5) * mm});
            skLineSegment(sketch, "E32.right", {"start": v(60.02, 57) * mm, "end": v(60.02, 53.5) * mm});
            skLineSegment(sketch, "E33.bottom", {"start": v(79.18, 57) * mm, "end": v(97.18, 57) * mm});
            skLineSegment(sketch, "E33.top", {"start": v(79.18, 53.5) * mm, "end": v(97.18, 53.5) * mm});
            skLineSegment(sketch, "E33.left", {"start": v(79.18, 57) * mm, "end": v(79.18, 53.5) * mm});
            skLineSegment(sketch, "E33.right", {"start": v(97.18, 57) * mm, "end": v(97.18, 53.5) * mm});
            skLineSegment(sketch, "E34.bottom", {"start": v(116.35, 57) * mm, "end": v(134.35, 57) * mm});
            skLineSegment(sketch, "E34.top", {"start": v(116.35, 53.5) * mm, "end": v(134.35, 53.5) * mm});
            skLineSegment(sketch, "E34.left", {"start": v(116.35, 57) * mm, "end": v(116.35, 53.5) * mm});
            skLineSegment(sketch, "E34.right", {"start": v(134.35, 57) * mm, "end": v(134.35, 53.5) * mm});
            skLineSegment(sketch, "E35", {"start": v(-14, 57) * mm, "end": v(4.85, 53.5) * mm, "construction": true});
            skLineSegment(sketch, "E36", {"start": v(22.85, 53.5) * mm, "end": v(42.02, 53.5) * mm, "construction": true});
            skLineSegment(sketch, "E37", {"start": v(60.02, 53.5) * mm, "end": v(79.18, 53.5) * mm, "construction": true});
            skLineSegment(sketch, "E38", {"start": v(97.18, 53.5) * mm, "end": v(116.35, 53.5) * mm, "construction": true});
            skLineSegment(sketch, "E39", {"start": v(134.35, 53.5) * mm, "end": v(153.2, 57) * mm, "construction": true});
            skLineSegment(sketch, "E40.bottom", {"start": v(-14, -8) * mm, "end": v(4.85, -8) * mm});
            skLineSegment(sketch, "E40.top", {"start": v(-14, -4.5) * mm, "end": v(4.85, -4.5) * mm});
            skLineSegment(sketch, "E40.left", {"start": v(-14, -8) * mm, "end": v(-14, -4.5) * mm});
            skLineSegment(sketch, "E40.right", {"start": v(4.85, -8) * mm, "end": v(4.85, -4.5) * mm});
            skLineSegment(sketch, "E41.bottom", {"start": v(22.85, -4.5) * mm, "end": v(42.02, -4.5) * mm});
            skLineSegment(sketch, "E41.top", {"start": v(22.85, -8) * mm, "end": v(42.02, -8) * mm});
            skLineSegment(sketch, "E41.left", {"start": v(22.85, -4.5) * mm, "end": v(22.85, -8) * mm});
            skLineSegment(sketch, "E41.right", {"start": v(42.02, -4.5) * mm, "end": v(42.02, -8) * mm});
            skLineSegment(sketch, "E42.bottom", {"start": v(60.02, -4.5) * mm, "end": v(79.18, -4.5) * mm});
            skLineSegment(sketch, "E42.top", {"start": v(60.02, -8) * mm, "end": v(79.18, -8) * mm});
            skLineSegment(sketch, "E42.left", {"start": v(60.02, -4.5) * mm, "end": v(60.02, -8) * mm});
            skLineSegment(sketch, "E42.right", {"start": v(79.18, -4.5) * mm, "end": v(79.18, -8) * mm});
            skLineSegment(sketch, "E43.bottom", {"start": v(97.18, -4.5) * mm, "end": v(116.35, -4.5) * mm});
            skLineSegment(sketch, "E43.top", {"start": v(97.18, -8) * mm, "end": v(116.35, -8) * mm});
            skLineSegment(sketch, "E43.left", {"start": v(97.18, -4.5) * mm, "end": v(97.18, -8) * mm});
            skLineSegment(sketch, "E43.right", {"start": v(116.35, -4.5) * mm, "end": v(116.35, -8) * mm});
            skLineSegment(sketch, "E44.bottom", {"start": v(134.35, -4.5) * mm, "end": v(153.2, -4.5) * mm});
            skLineSegment(sketch, "E44.top", {"start": v(134.35, -8) * mm, "end": v(153.2, -8) * mm});
            skLineSegment(sketch, "E44.left", {"start": v(134.35, -4.5) * mm, "end": v(134.35, -8) * mm});
            skLineSegment(sketch, "E44.right", {"start": v(153.2, -4.5) * mm, "end": v(153.2, -8) * mm});
            skLineSegment(sketch, "E45.bottom", {"start": v(143.7, 13) * mm, "end": v(146.7, 13) * mm});
            skLineSegment(sketch, "E45.top", {"start": v(143.7, -1) * mm, "end": v(146.7, -1) * mm});
            skLineSegment(sketch, "E45.left", {"start": v(143.7, 13) * mm, "end": v(143.7, -1) * mm});
            skLineSegment(sketch, "E45.right", {"start": v(146.7, 13) * mm, "end": v(146.7, -1) * mm});
            skLineSegment(sketch, "E46", {"start": v(-10.5, 33.5) * mm, "end": v(-4.5, 36) * mm, "construction": true});
            skLineSegment(sketch, "E47", {"start": v(-10.5, 15.5) * mm, "end": v(-4.5, 13) * mm, "construction": true});
            skSolve(sketch);
        }
        {
            var Q0;
            Q0=qSketchRegion(id+"F4",true);
            extrude(context, id + "F5", {"entities" : qUnion([Q0]), "operationType" : NewBodyOperationType.REMOVE, "oppositeDirection" : true, "depth" : 25 * mm, "offsetDistance" : 25 * mm});
        }
    });
